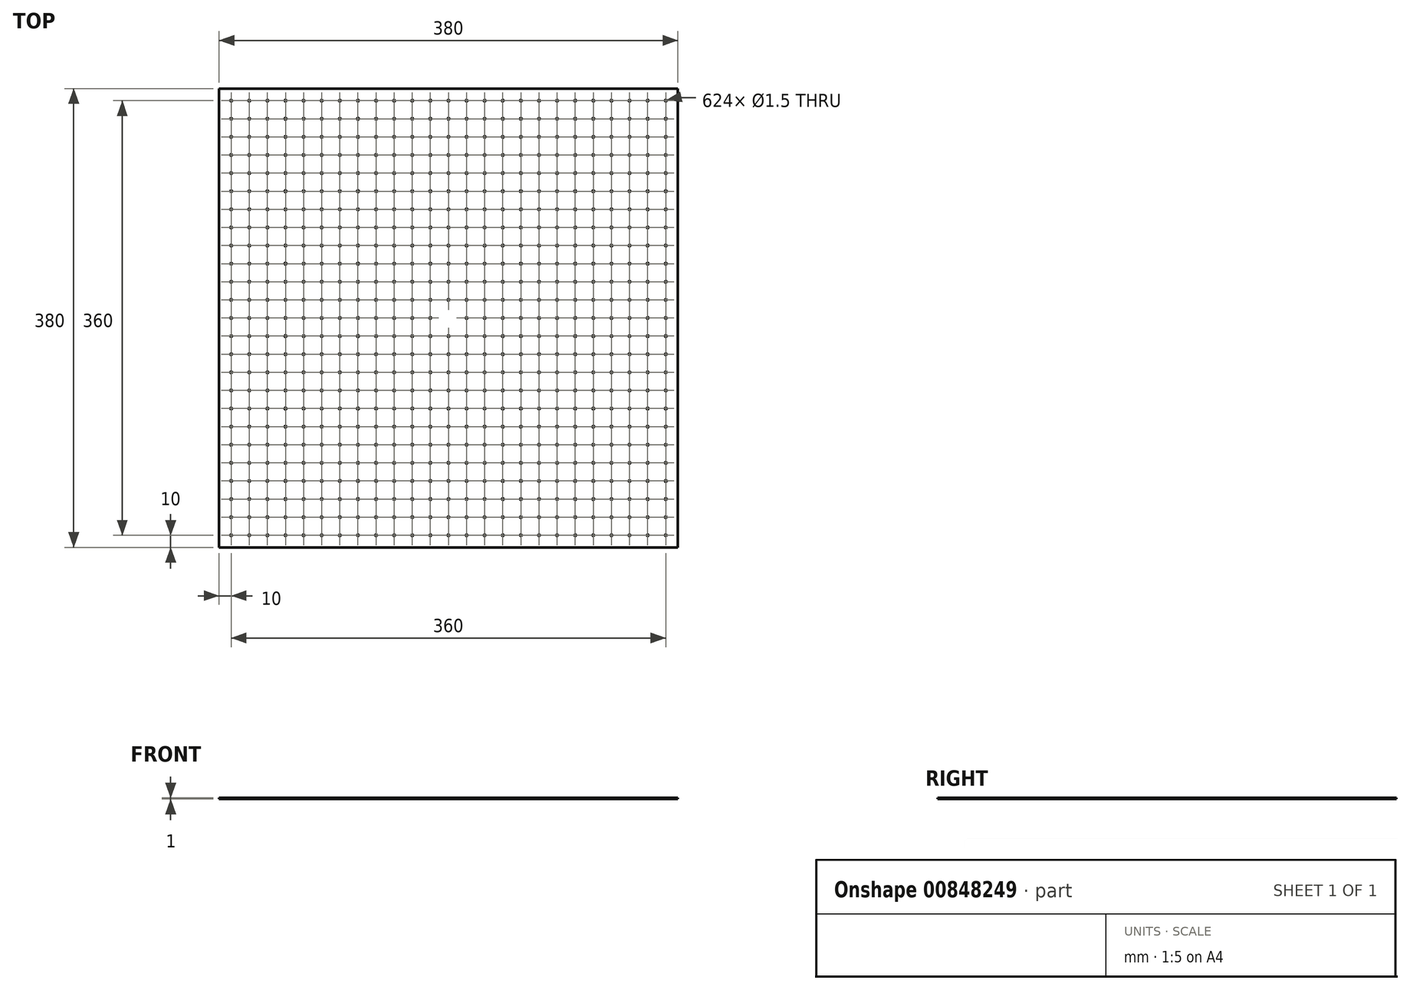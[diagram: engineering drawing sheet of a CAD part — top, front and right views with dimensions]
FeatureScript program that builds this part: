
annotation { "Feature Type Name" : "Feature", "Feature Type Description" : "" }
export const myFeature = defineFeature(function(context is Context, id is Id, definition is map)
    precondition{}
    {
        {
            var Q0;
            Q0=qCreatedBy(makeId("Top.planeOp"),FACE);
            var sketch = newSketch(context, id + "F0", { "sketchPlane" : qUnion([Q0])});
            skLineSegment(sketch, "E0.bottom", {"start": v(-190, -190) * mm, "end": v(190, -190) * mm});
            skLineSegment(sketch, "E0.top", {"start": v(-190, 190) * mm, "end": v(190, 190) * mm});
            skLineSegment(sketch, "E0.left", {"start": v(-190, -190) * mm, "end": v(-190, 190) * mm});
            skLineSegment(sketch, "E0.right", {"start": v(190, -190) * mm, "end": v(190, 190) * mm});
            skPoint(sketch, "E0.middle", {"position": v(0, 0) * mm});
            skSolve(sketch);
        }
        {
            var Q0;
            Q0 = qSketchRegion(id + "F0", true);
            extrude(context, id + "F1", {"entities" : qUnion([Q0]), "depth" : 1 * mm, "offsetDistance" : 25 * mm});
        }
        {
            var Q0;
            Q0=makeQuery(id+"F1.opExtrude","CAP_FACE",FACE,{"disambiguationData":[OSD([sQuery(id+"F0.wireOp",EDGE,"E0.bottom"),sQuery(id+"F0.wireOp",EDGE,"E0.top"),sQuery(id+"F0.wireOp",EDGE,"E0.left"),sQuery(id+"F0.wireOp",EDGE,"E0.right")])],"isStart":false});
            var sketch = newSketch(context, id + "F2", { "sketchPlane" : qUnion([Q0])});
            skCircle(sketch, "E1", {"center": v(-180, 180) * mm, "radius": 0.75 * mm});
            skCircle(sketch, "E2.1.0.0", {"center": v(-165, 180) * mm, "radius": 0.75 * mm});
            skCircle(sketch, "E2.2.0.0", {"center": v(-150, 180) * mm, "radius": 0.75 * mm});
            skCircle(sketch, "E2.3.0.0", {"center": v(-135, 180) * mm, "radius": 0.75 * mm});
            skCircle(sketch, "E2.4.0.0", {"center": v(-120, 180) * mm, "radius": 0.75 * mm});
            skCircle(sketch, "E2.5.0.0", {"center": v(-105, 180) * mm, "radius": 0.75 * mm});
            skCircle(sketch, "E2.6.0.0", {"center": v(-90, 180) * mm, "radius": 0.75 * mm});
            skCircle(sketch, "E2.7.0.0", {"center": v(-75, 180) * mm, "radius": 0.75 * mm});
            skCircle(sketch, "E2.8.0.0", {"center": v(-60, 180) * mm, "radius": 0.75 * mm});
            skCircle(sketch, "E2.9.0.0", {"center": v(-45, 180) * mm, "radius": 0.75 * mm});
            skCircle(sketch, "E2.10.0.0", {"center": v(-30, 180) * mm, "radius": 0.75 * mm});
            skCircle(sketch, "E2.11.0.0", {"center": v(-15, 180) * mm, "radius": 0.75 * mm});
            skCircle(sketch, "E2.12.0.0", {"center": v(0, 180) * mm, "radius": 0.75 * mm});
            skCircle(sketch, "E2.13.0.0", {"center": v(15, 180) * mm, "radius": 0.75 * mm});
            skCircle(sketch, "E2.14.0.0", {"center": v(30, 180) * mm, "radius": 0.75 * mm});
            skCircle(sketch, "E2.15.0.0", {"center": v(45, 180) * mm, "radius": 0.75 * mm});
            skCircle(sketch, "E2.16.0.0", {"center": v(60, 180) * mm, "radius": 0.75 * mm});
            skCircle(sketch, "E2.17.0.0", {"center": v(75, 180) * mm, "radius": 0.75 * mm});
            skCircle(sketch, "E2.18.0.0", {"center": v(90, 180) * mm, "radius": 0.75 * mm});
            skCircle(sketch, "E2.19.0.0", {"center": v(105, 180) * mm, "radius": 0.75 * mm});
            skCircle(sketch, "E2.20.0.0", {"center": v(120, 180) * mm, "radius": 0.75 * mm});
            skCircle(sketch, "E2.21.0.0", {"center": v(135, 180) * mm, "radius": 0.75 * mm});
            skCircle(sketch, "E2.22.0.0", {"center": v(150, 180) * mm, "radius": 0.75 * mm});
            skCircle(sketch, "E2.23.0.0", {"center": v(165, 180) * mm, "radius": 0.75 * mm});
            skCircle(sketch, "E2.24.0.0", {"center": v(180, 180) * mm, "radius": 0.75 * mm});
            skCircle(sketch, "E2.25.0.0", {"center": v(195, 180) * mm, "radius": 0.75 * mm});
            skCircle(sketch, "E2.26.0.0", {"center": v(210, 180) * mm, "radius": 0.75 * mm});
            skCircle(sketch, "E2.27.0.0", {"center": v(225, 180) * mm, "radius": 0.75 * mm});
            skCircle(sketch, "E2.28.0.0", {"center": v(240, 180) * mm, "radius": 0.75 * mm});
            skCircle(sketch, "E2.29.0.0", {"center": v(255, 180) * mm, "radius": 0.75 * mm});
            skCircle(sketch, "E2.30.0.0", {"center": v(270, 180) * mm, "radius": 0.75 * mm});
            skCircle(sketch, "E2.31.0.0", {"center": v(285, 180) * mm, "radius": 0.75 * mm});
            skCircle(sketch, "E2.32.0.0", {"center": v(300, 180) * mm, "radius": 0.75 * mm});
            skCircle(sketch, "E2.33.0.0", {"center": v(315, 180) * mm, "radius": 0.75 * mm});
            skCircle(sketch, "E2.34.0.0", {"center": v(330, 180) * mm, "radius": 0.75 * mm});
            skCircle(sketch, "E2.35.0.0", {"center": v(345, 180) * mm, "radius": 0.75 * mm});
            skLineSegment(sketch, "E2.direction1", {"start": v(-180, 180) * mm, "end": v(-165, 180) * mm, "construction": true});
            skCircle(sketch, "E3.0.1.0", {"center": v(-180, 165) * mm, "radius": 0.75 * mm});
            skCircle(sketch, "E3.0.1.1", {"center": v(-165, 165) * mm, "radius": 0.75 * mm});
            skCircle(sketch, "E3.0.1.2", {"center": v(-150, 165) * mm, "radius": 0.75 * mm});
            skCircle(sketch, "E3.0.1.3", {"center": v(-135, 165) * mm, "radius": 0.75 * mm});
            skCircle(sketch, "E3.0.1.4", {"center": v(-120, 165) * mm, "radius": 0.75 * mm});
            skCircle(sketch, "E3.0.1.5", {"center": v(-105, 165) * mm, "radius": 0.75 * mm});
            skCircle(sketch, "E3.0.1.6", {"center": v(-90, 165) * mm, "radius": 0.75 * mm});
            skCircle(sketch, "E3.0.1.7", {"center": v(-75, 165) * mm, "radius": 0.75 * mm});
            skCircle(sketch, "E3.0.1.8", {"center": v(-60, 165) * mm, "radius": 0.75 * mm});
            skCircle(sketch, "E3.0.1.9", {"center": v(-45, 165) * mm, "radius": 0.75 * mm});
            skCircle(sketch, "E3.0.1.10", {"center": v(-30, 165) * mm, "radius": 0.75 * mm});
            skCircle(sketch, "E3.0.1.11", {"center": v(-15, 165) * mm, "radius": 0.75 * mm});
            skCircle(sketch, "E3.0.1.12", {"center": v(0, 165) * mm, "radius": 0.75 * mm});
            skCircle(sketch, "E3.0.1.13", {"center": v(15, 165) * mm, "radius": 0.75 * mm});
            skCircle(sketch, "E3.0.1.14", {"center": v(30, 165) * mm, "radius": 0.75 * mm});
            skCircle(sketch, "E3.0.1.15", {"center": v(45, 165) * mm, "radius": 0.75 * mm});
            skCircle(sketch, "E3.0.1.16", {"center": v(60, 165) * mm, "radius": 0.75 * mm});
            skCircle(sketch, "E3.0.1.17", {"center": v(75, 165) * mm, "radius": 0.75 * mm});
            skCircle(sketch, "E3.0.1.18", {"center": v(90, 165) * mm, "radius": 0.75 * mm});
            skCircle(sketch, "E3.0.1.19", {"center": v(105, 165) * mm, "radius": 0.75 * mm});
            skCircle(sketch, "E3.0.1.20", {"center": v(120, 165) * mm, "radius": 0.75 * mm});
            skCircle(sketch, "E3.0.1.21", {"center": v(135, 165) * mm, "radius": 0.75 * mm});
            skCircle(sketch, "E3.0.1.22", {"center": v(150, 165) * mm, "radius": 0.75 * mm});
            skCircle(sketch, "E3.0.1.23", {"center": v(165, 165) * mm, "radius": 0.75 * mm});
            skCircle(sketch, "E3.0.1.24", {"center": v(180, 165) * mm, "radius": 0.75 * mm});
            skCircle(sketch, "E3.0.1.25", {"center": v(195, 165) * mm, "radius": 0.75 * mm});
            skCircle(sketch, "E3.0.1.26", {"center": v(210, 165) * mm, "radius": 0.75 * mm});
            skCircle(sketch, "E3.0.1.27", {"center": v(225, 165) * mm, "radius": 0.75 * mm});
            skCircle(sketch, "E3.0.1.28", {"center": v(240, 165) * mm, "radius": 0.75 * mm});
            skCircle(sketch, "E3.0.1.29", {"center": v(255, 165) * mm, "radius": 0.75 * mm});
            skCircle(sketch, "E3.0.1.30", {"center": v(270, 165) * mm, "radius": 0.75 * mm});
            skCircle(sketch, "E3.0.1.31", {"center": v(285, 165) * mm, "radius": 0.75 * mm});
            skCircle(sketch, "E3.0.1.32", {"center": v(300, 165) * mm, "radius": 0.75 * mm});
            skCircle(sketch, "E3.0.1.33", {"center": v(315, 165) * mm, "radius": 0.75 * mm});
            skCircle(sketch, "E3.0.1.34", {"center": v(345, 165) * mm, "radius": 0.75 * mm});
            skCircle(sketch, "E3.0.1.35", {"center": v(330, 165) * mm, "radius": 0.75 * mm});
            skLineSegment(sketch, "E3.direction1", {"start": v(-180, 180) * mm, "end": v(25, 180) * mm, "construction": true});
            skLineSegment(sketch, "E3.direction2", {"start": v(-180, 165) * mm, "end": v(-180, 180) * mm, "construction": true});
            skCircle(sketch, "E4.0.0.2", {"center": v(-180, 150) * mm, "radius": 0.75 * mm});
            skCircle(sketch, "E4.2.0.2", {"center": v(-165, 150) * mm, "radius": 0.75 * mm});
            skCircle(sketch, "E4.4.0.2", {"center": v(-150, 150) * mm, "radius": 0.75 * mm});
            skCircle(sketch, "E4.6.0.2", {"center": v(-135, 150) * mm, "radius": 0.75 * mm});
            skCircle(sketch, "E4.8.0.2", {"center": v(-120, 150) * mm, "radius": 0.75 * mm});
            skCircle(sketch, "E4.10.0.2", {"center": v(-105, 150) * mm, "radius": 0.75 * mm});
            skCircle(sketch, "E4.12.0.2", {"center": v(-90, 150) * mm, "radius": 0.75 * mm});
            skCircle(sketch, "E4.14.0.2", {"center": v(-75, 150) * mm, "radius": 0.75 * mm});
            skCircle(sketch, "E4.16.0.2", {"center": v(-60, 150) * mm, "radius": 0.75 * mm});
            skCircle(sketch, "E4.18.0.2", {"center": v(-45, 150) * mm, "radius": 0.75 * mm});
            skCircle(sketch, "E4.20.0.2", {"center": v(-30, 150) * mm, "radius": 0.75 * mm});
            skCircle(sketch, "E4.22.0.2", {"center": v(-15, 150) * mm, "radius": 0.75 * mm});
            skCircle(sketch, "E4.24.0.2", {"center": v(0, 150) * mm, "radius": 0.75 * mm});
            skCircle(sketch, "E4.26.0.2", {"center": v(15, 150) * mm, "radius": 0.75 * mm});
            skCircle(sketch, "E4.28.0.2", {"center": v(30, 150) * mm, "radius": 0.75 * mm});
            skCircle(sketch, "E4.30.0.2", {"center": v(45, 150) * mm, "radius": 0.75 * mm});
            skCircle(sketch, "E4.32.0.2", {"center": v(60, 150) * mm, "radius": 0.75 * mm});
            skCircle(sketch, "E4.34.0.2", {"center": v(75, 150) * mm, "radius": 0.75 * mm});
            skCircle(sketch, "E4.36.0.2", {"center": v(90, 150) * mm, "radius": 0.75 * mm});
            skCircle(sketch, "E4.38.0.2", {"center": v(105, 150) * mm, "radius": 0.75 * mm});
            skCircle(sketch, "E4.40.0.2", {"center": v(120, 150) * mm, "radius": 0.75 * mm});
            skCircle(sketch, "E4.42.0.2", {"center": v(135, 150) * mm, "radius": 0.75 * mm});
            skCircle(sketch, "E4.44.0.2", {"center": v(150, 150) * mm, "radius": 0.75 * mm});
            skCircle(sketch, "E4.46.0.2", {"center": v(165, 150) * mm, "radius": 0.75 * mm});
            skCircle(sketch, "E4.48.0.2", {"center": v(180, 150) * mm, "radius": 0.75 * mm});
            skCircle(sketch, "E4.50.0.2", {"center": v(195, 150) * mm, "radius": 0.75 * mm});
            skCircle(sketch, "E4.52.0.2", {"center": v(210, 150) * mm, "radius": 0.75 * mm});
            skCircle(sketch, "E4.54.0.2", {"center": v(225, 150) * mm, "radius": 0.75 * mm});
            skCircle(sketch, "E4.56.0.2", {"center": v(240, 150) * mm, "radius": 0.75 * mm});
            skCircle(sketch, "E4.58.0.2", {"center": v(255, 150) * mm, "radius": 0.75 * mm});
            skCircle(sketch, "E4.60.0.2", {"center": v(270, 150) * mm, "radius": 0.75 * mm});
            skCircle(sketch, "E4.62.0.2", {"center": v(285, 150) * mm, "radius": 0.75 * mm});
            skCircle(sketch, "E4.64.0.2", {"center": v(300, 150) * mm, "radius": 0.75 * mm});
            skCircle(sketch, "E4.66.0.2", {"center": v(315, 150) * mm, "radius": 0.75 * mm});
            skCircle(sketch, "E4.68.0.2", {"center": v(345, 150) * mm, "radius": 0.75 * mm});
            skCircle(sketch, "E4.70.0.2", {"center": v(330, 150) * mm, "radius": 0.75 * mm});
            skCircle(sketch, "E4.0.0.3", {"center": v(-180, 135) * mm, "radius": 0.75 * mm});
            skCircle(sketch, "E4.2.0.3", {"center": v(-165, 135) * mm, "radius": 0.75 * mm});
            skCircle(sketch, "E4.4.0.3", {"center": v(-150, 135) * mm, "radius": 0.75 * mm});
            skCircle(sketch, "E4.6.0.3", {"center": v(-135, 135) * mm, "radius": 0.75 * mm});
            skCircle(sketch, "E4.8.0.3", {"center": v(-120, 135) * mm, "radius": 0.75 * mm});
            skCircle(sketch, "E4.10.0.3", {"center": v(-105, 135) * mm, "radius": 0.75 * mm});
            skCircle(sketch, "E4.12.0.3", {"center": v(-90, 135) * mm, "radius": 0.75 * mm});
            skCircle(sketch, "E4.14.0.3", {"center": v(-75, 135) * mm, "radius": 0.75 * mm});
            skCircle(sketch, "E4.16.0.3", {"center": v(-60, 135) * mm, "radius": 0.75 * mm});
            skCircle(sketch, "E4.18.0.3", {"center": v(-45, 135) * mm, "radius": 0.75 * mm});
            skCircle(sketch, "E4.20.0.3", {"center": v(-30, 135) * mm, "radius": 0.75 * mm});
            skCircle(sketch, "E4.22.0.3", {"center": v(-15, 135) * mm, "radius": 0.75 * mm});
            skCircle(sketch, "E4.24.0.3", {"center": v(0, 135) * mm, "radius": 0.75 * mm});
            skCircle(sketch, "E4.26.0.3", {"center": v(15, 135) * mm, "radius": 0.75 * mm});
            skCircle(sketch, "E4.28.0.3", {"center": v(30, 135) * mm, "radius": 0.75 * mm});
            skCircle(sketch, "E4.30.0.3", {"center": v(45, 135) * mm, "radius": 0.75 * mm});
            skCircle(sketch, "E4.32.0.3", {"center": v(60, 135) * mm, "radius": 0.75 * mm});
            skCircle(sketch, "E4.34.0.3", {"center": v(75, 135) * mm, "radius": 0.75 * mm});
            skCircle(sketch, "E4.36.0.3", {"center": v(90, 135) * mm, "radius": 0.75 * mm});
            skCircle(sketch, "E4.38.0.3", {"center": v(105, 135) * mm, "radius": 0.75 * mm});
            skCircle(sketch, "E4.40.0.3", {"center": v(120, 135) * mm, "radius": 0.75 * mm});
            skCircle(sketch, "E4.42.0.3", {"center": v(135, 135) * mm, "radius": 0.75 * mm});
            skCircle(sketch, "E4.44.0.3", {"center": v(150, 135) * mm, "radius": 0.75 * mm});
            skCircle(sketch, "E4.46.0.3", {"center": v(165, 135) * mm, "radius": 0.75 * mm});
            skCircle(sketch, "E4.48.0.3", {"center": v(180, 135) * mm, "radius": 0.75 * mm});
            skCircle(sketch, "E4.50.0.3", {"center": v(195, 135) * mm, "radius": 0.75 * mm});
            skCircle(sketch, "E4.52.0.3", {"center": v(210, 135) * mm, "radius": 0.75 * mm});
            skCircle(sketch, "E4.54.0.3", {"center": v(225, 135) * mm, "radius": 0.75 * mm});
            skCircle(sketch, "E4.56.0.3", {"center": v(240, 135) * mm, "radius": 0.75 * mm});
            skCircle(sketch, "E4.58.0.3", {"center": v(255, 135) * mm, "radius": 0.75 * mm});
            skCircle(sketch, "E4.60.0.3", {"center": v(270, 135) * mm, "radius": 0.75 * mm});
            skCircle(sketch, "E4.62.0.3", {"center": v(285, 135) * mm, "radius": 0.75 * mm});
            skCircle(sketch, "E4.64.0.3", {"center": v(300, 135) * mm, "radius": 0.75 * mm});
            skCircle(sketch, "E4.66.0.3", {"center": v(315, 135) * mm, "radius": 0.75 * mm});
            skCircle(sketch, "E4.68.0.3", {"center": v(345, 135) * mm, "radius": 0.75 * mm});
            skCircle(sketch, "E4.70.0.3", {"center": v(330, 135) * mm, "radius": 0.75 * mm});
            skCircle(sketch, "E4.0.0.4", {"center": v(-180, 120) * mm, "radius": 0.75 * mm});
            skCircle(sketch, "E4.2.0.4", {"center": v(-165, 120) * mm, "radius": 0.75 * mm});
            skCircle(sketch, "E4.4.0.4", {"center": v(-150, 120) * mm, "radius": 0.75 * mm});
            skCircle(sketch, "E4.6.0.4", {"center": v(-135, 120) * mm, "radius": 0.75 * mm});
            skCircle(sketch, "E4.8.0.4", {"center": v(-120, 120) * mm, "radius": 0.75 * mm});
            skCircle(sketch, "E4.10.0.4", {"center": v(-105, 120) * mm, "radius": 0.75 * mm});
            skCircle(sketch, "E4.12.0.4", {"center": v(-90, 120) * mm, "radius": 0.75 * mm});
            skCircle(sketch, "E4.14.0.4", {"center": v(-75, 120) * mm, "radius": 0.75 * mm});
            skCircle(sketch, "E4.16.0.4", {"center": v(-60, 120) * mm, "radius": 0.75 * mm});
            skCircle(sketch, "E4.18.0.4", {"center": v(-45, 120) * mm, "radius": 0.75 * mm});
            skCircle(sketch, "E4.20.0.4", {"center": v(-30, 120) * mm, "radius": 0.75 * mm});
            skCircle(sketch, "E4.22.0.4", {"center": v(-15, 120) * mm, "radius": 0.75 * mm});
            skCircle(sketch, "E4.24.0.4", {"center": v(0, 120) * mm, "radius": 0.75 * mm});
            skCircle(sketch, "E4.26.0.4", {"center": v(15, 120) * mm, "radius": 0.75 * mm});
            skCircle(sketch, "E4.28.0.4", {"center": v(30, 120) * mm, "radius": 0.75 * mm});
            skCircle(sketch, "E4.30.0.4", {"center": v(45, 120) * mm, "radius": 0.75 * mm});
            skCircle(sketch, "E4.32.0.4", {"center": v(60, 120) * mm, "radius": 0.75 * mm});
            skCircle(sketch, "E4.34.0.4", {"center": v(75, 120) * mm, "radius": 0.75 * mm});
            skCircle(sketch, "E4.36.0.4", {"center": v(90, 120) * mm, "radius": 0.75 * mm});
            skCircle(sketch, "E4.38.0.4", {"center": v(105, 120) * mm, "radius": 0.75 * mm});
            skCircle(sketch, "E4.40.0.4", {"center": v(120, 120) * mm, "radius": 0.75 * mm});
            skCircle(sketch, "E4.42.0.4", {"center": v(135, 120) * mm, "radius": 0.75 * mm});
            skCircle(sketch, "E4.44.0.4", {"center": v(150, 120) * mm, "radius": 0.75 * mm});
            skCircle(sketch, "E4.46.0.4", {"center": v(165, 120) * mm, "radius": 0.75 * mm});
            skCircle(sketch, "E4.48.0.4", {"center": v(180, 120) * mm, "radius": 0.75 * mm});
            skCircle(sketch, "E4.50.0.4", {"center": v(195, 120) * mm, "radius": 0.75 * mm});
            skCircle(sketch, "E4.52.0.4", {"center": v(210, 120) * mm, "radius": 0.75 * mm});
            skCircle(sketch, "E4.54.0.4", {"center": v(225, 120) * mm, "radius": 0.75 * mm});
            skCircle(sketch, "E4.56.0.4", {"center": v(240, 120) * mm, "radius": 0.75 * mm});
            skCircle(sketch, "E4.58.0.4", {"center": v(255, 120) * mm, "radius": 0.75 * mm});
            skCircle(sketch, "E4.60.0.4", {"center": v(270, 120) * mm, "radius": 0.75 * mm});
            skCircle(sketch, "E4.62.0.4", {"center": v(285, 120) * mm, "radius": 0.75 * mm});
            skCircle(sketch, "E4.64.0.4", {"center": v(300, 120) * mm, "radius": 0.75 * mm});
            skCircle(sketch, "E4.66.0.4", {"center": v(315, 120) * mm, "radius": 0.75 * mm});
            skCircle(sketch, "E4.68.0.4", {"center": v(345, 120) * mm, "radius": 0.75 * mm});
            skCircle(sketch, "E4.70.0.4", {"center": v(330, 120) * mm, "radius": 0.75 * mm});
            skCircle(sketch, "E4.0.0.5", {"center": v(-180, 105) * mm, "radius": 0.75 * mm});
            skCircle(sketch, "E4.2.0.5", {"center": v(-165, 105) * mm, "radius": 0.75 * mm});
            skCircle(sketch, "E4.4.0.5", {"center": v(-150, 105) * mm, "radius": 0.75 * mm});
            skCircle(sketch, "E4.6.0.5", {"center": v(-135, 105) * mm, "radius": 0.75 * mm});
            skCircle(sketch, "E4.8.0.5", {"center": v(-120, 105) * mm, "radius": 0.75 * mm});
            skCircle(sketch, "E4.10.0.5", {"center": v(-105, 105) * mm, "radius": 0.75 * mm});
            skCircle(sketch, "E4.12.0.5", {"center": v(-90, 105) * mm, "radius": 0.75 * mm});
            skCircle(sketch, "E4.14.0.5", {"center": v(-75, 105) * mm, "radius": 0.75 * mm});
            skCircle(sketch, "E4.16.0.5", {"center": v(-60, 105) * mm, "radius": 0.75 * mm});
            skCircle(sketch, "E4.18.0.5", {"center": v(-45, 105) * mm, "radius": 0.75 * mm});
            skCircle(sketch, "E4.20.0.5", {"center": v(-30, 105) * mm, "radius": 0.75 * mm});
            skCircle(sketch, "E4.22.0.5", {"center": v(-15, 105) * mm, "radius": 0.75 * mm});
            skCircle(sketch, "E4.24.0.5", {"center": v(0, 105) * mm, "radius": 0.75 * mm});
            skCircle(sketch, "E4.26.0.5", {"center": v(15, 105) * mm, "radius": 0.75 * mm});
            skCircle(sketch, "E4.28.0.5", {"center": v(30, 105) * mm, "radius": 0.75 * mm});
            skCircle(sketch, "E4.30.0.5", {"center": v(45, 105) * mm, "radius": 0.75 * mm});
            skCircle(sketch, "E4.32.0.5", {"center": v(60, 105) * mm, "radius": 0.75 * mm});
            skCircle(sketch, "E4.34.0.5", {"center": v(75, 105) * mm, "radius": 0.75 * mm});
            skCircle(sketch, "E4.36.0.5", {"center": v(90, 105) * mm, "radius": 0.75 * mm});
            skCircle(sketch, "E4.38.0.5", {"center": v(105, 105) * mm, "radius": 0.75 * mm});
            skCircle(sketch, "E4.40.0.5", {"center": v(120, 105) * mm, "radius": 0.75 * mm});
            skCircle(sketch, "E4.42.0.5", {"center": v(135, 105) * mm, "radius": 0.75 * mm});
            skCircle(sketch, "E4.44.0.5", {"center": v(150, 105) * mm, "radius": 0.75 * mm});
            skCircle(sketch, "E4.46.0.5", {"center": v(165, 105) * mm, "radius": 0.75 * mm});
            skCircle(sketch, "E4.48.0.5", {"center": v(180, 105) * mm, "radius": 0.75 * mm});
            skCircle(sketch, "E4.50.0.5", {"center": v(195, 105) * mm, "radius": 0.75 * mm});
            skCircle(sketch, "E4.52.0.5", {"center": v(210, 105) * mm, "radius": 0.75 * mm});
            skCircle(sketch, "E4.54.0.5", {"center": v(225, 105) * mm, "radius": 0.75 * mm});
            skCircle(sketch, "E4.56.0.5", {"center": v(240, 105) * mm, "radius": 0.75 * mm});
            skCircle(sketch, "E4.58.0.5", {"center": v(255, 105) * mm, "radius": 0.75 * mm});
            skCircle(sketch, "E4.60.0.5", {"center": v(270, 105) * mm, "radius": 0.75 * mm});
            skCircle(sketch, "E4.62.0.5", {"center": v(285, 105) * mm, "radius": 0.75 * mm});
            skCircle(sketch, "E4.64.0.5", {"center": v(300, 105) * mm, "radius": 0.75 * mm});
            skCircle(sketch, "E4.66.0.5", {"center": v(315, 105) * mm, "radius": 0.75 * mm});
            skCircle(sketch, "E4.68.0.5", {"center": v(345, 105) * mm, "radius": 0.75 * mm});
            skCircle(sketch, "E4.70.0.5", {"center": v(330, 105) * mm, "radius": 0.75 * mm});
            skCircle(sketch, "E4.0.0.6", {"center": v(-180, 90) * mm, "radius": 0.75 * mm});
            skCircle(sketch, "E4.2.0.6", {"center": v(-165, 90) * mm, "radius": 0.75 * mm});
            skCircle(sketch, "E4.4.0.6", {"center": v(-150, 90) * mm, "radius": 0.75 * mm});
            skCircle(sketch, "E4.6.0.6", {"center": v(-135, 90) * mm, "radius": 0.75 * mm});
            skCircle(sketch, "E4.8.0.6", {"center": v(-120, 90) * mm, "radius": 0.75 * mm});
            skCircle(sketch, "E4.10.0.6", {"center": v(-105, 90) * mm, "radius": 0.75 * mm});
            skCircle(sketch, "E4.12.0.6", {"center": v(-90, 90) * mm, "radius": 0.75 * mm});
            skCircle(sketch, "E4.14.0.6", {"center": v(-75, 90) * mm, "radius": 0.75 * mm});
            skCircle(sketch, "E4.16.0.6", {"center": v(-60, 90) * mm, "radius": 0.75 * mm});
            skCircle(sketch, "E4.18.0.6", {"center": v(-45, 90) * mm, "radius": 0.75 * mm});
            skCircle(sketch, "E4.20.0.6", {"center": v(-30, 90) * mm, "radius": 0.75 * mm});
            skCircle(sketch, "E4.22.0.6", {"center": v(-15, 90) * mm, "radius": 0.75 * mm});
            skCircle(sketch, "E4.24.0.6", {"center": v(0, 90) * mm, "radius": 0.75 * mm});
            skCircle(sketch, "E4.26.0.6", {"center": v(15, 90) * mm, "radius": 0.75 * mm});
            skCircle(sketch, "E4.28.0.6", {"center": v(30, 90) * mm, "radius": 0.75 * mm});
            skCircle(sketch, "E4.30.0.6", {"center": v(45, 90) * mm, "radius": 0.75 * mm});
            skCircle(sketch, "E4.32.0.6", {"center": v(60, 90) * mm, "radius": 0.75 * mm});
            skCircle(sketch, "E4.34.0.6", {"center": v(75, 90) * mm, "radius": 0.75 * mm});
            skCircle(sketch, "E4.36.0.6", {"center": v(90, 90) * mm, "radius": 0.75 * mm});
            skCircle(sketch, "E4.38.0.6", {"center": v(105, 90) * mm, "radius": 0.75 * mm});
            skCircle(sketch, "E4.40.0.6", {"center": v(120, 90) * mm, "radius": 0.75 * mm});
            skCircle(sketch, "E4.42.0.6", {"center": v(135, 90) * mm, "radius": 0.75 * mm});
            skCircle(sketch, "E4.44.0.6", {"center": v(150, 90) * mm, "radius": 0.75 * mm});
            skCircle(sketch, "E4.46.0.6", {"center": v(165, 90) * mm, "radius": 0.75 * mm});
            skCircle(sketch, "E4.48.0.6", {"center": v(180, 90) * mm, "radius": 0.75 * mm});
            skCircle(sketch, "E4.50.0.6", {"center": v(195, 90) * mm, "radius": 0.75 * mm});
            skCircle(sketch, "E4.52.0.6", {"center": v(210, 90) * mm, "radius": 0.75 * mm});
            skCircle(sketch, "E4.54.0.6", {"center": v(225, 90) * mm, "radius": 0.75 * mm});
            skCircle(sketch, "E4.56.0.6", {"center": v(240, 90) * mm, "radius": 0.75 * mm});
            skCircle(sketch, "E4.58.0.6", {"center": v(255, 90) * mm, "radius": 0.75 * mm});
            skCircle(sketch, "E4.60.0.6", {"center": v(270, 90) * mm, "radius": 0.75 * mm});
            skCircle(sketch, "E4.62.0.6", {"center": v(285, 90) * mm, "radius": 0.75 * mm});
            skCircle(sketch, "E4.64.0.6", {"center": v(300, 90) * mm, "radius": 0.75 * mm});
            skCircle(sketch, "E4.66.0.6", {"center": v(315, 90) * mm, "radius": 0.75 * mm});
            skCircle(sketch, "E4.68.0.6", {"center": v(345, 90) * mm, "radius": 0.75 * mm});
            skCircle(sketch, "E4.70.0.6", {"center": v(330, 90) * mm, "radius": 0.75 * mm});
            skCircle(sketch, "E4.0.0.7", {"center": v(-180, 75) * mm, "radius": 0.75 * mm});
            skCircle(sketch, "E4.2.0.7", {"center": v(-165, 75) * mm, "radius": 0.75 * mm});
            skCircle(sketch, "E4.4.0.7", {"center": v(-150, 75) * mm, "radius": 0.75 * mm});
            skCircle(sketch, "E4.6.0.7", {"center": v(-135, 75) * mm, "radius": 0.75 * mm});
            skCircle(sketch, "E4.8.0.7", {"center": v(-120, 75) * mm, "radius": 0.75 * mm});
            skCircle(sketch, "E4.10.0.7", {"center": v(-105, 75) * mm, "radius": 0.75 * mm});
            skCircle(sketch, "E4.12.0.7", {"center": v(-90, 75) * mm, "radius": 0.75 * mm});
            skCircle(sketch, "E4.14.0.7", {"center": v(-75, 75) * mm, "radius": 0.75 * mm});
            skCircle(sketch, "E4.16.0.7", {"center": v(-60, 75) * mm, "radius": 0.75 * mm});
            skCircle(sketch, "E4.18.0.7", {"center": v(-45, 75) * mm, "radius": 0.75 * mm});
            skCircle(sketch, "E4.20.0.7", {"center": v(-30, 75) * mm, "radius": 0.75 * mm});
            skCircle(sketch, "E4.22.0.7", {"center": v(-15, 75) * mm, "radius": 0.75 * mm});
            skCircle(sketch, "E4.24.0.7", {"center": v(0, 75) * mm, "radius": 0.75 * mm});
            skCircle(sketch, "E4.26.0.7", {"center": v(15, 75) * mm, "radius": 0.75 * mm});
            skCircle(sketch, "E4.28.0.7", {"center": v(30, 75) * mm, "radius": 0.75 * mm});
            skCircle(sketch, "E4.30.0.7", {"center": v(45, 75) * mm, "radius": 0.75 * mm});
            skCircle(sketch, "E4.32.0.7", {"center": v(60, 75) * mm, "radius": 0.75 * mm});
            skCircle(sketch, "E4.34.0.7", {"center": v(75, 75) * mm, "radius": 0.75 * mm});
            skCircle(sketch, "E4.36.0.7", {"center": v(90, 75) * mm, "radius": 0.75 * mm});
            skCircle(sketch, "E4.38.0.7", {"center": v(105, 75) * mm, "radius": 0.75 * mm});
            skCircle(sketch, "E4.40.0.7", {"center": v(120, 75) * mm, "radius": 0.75 * mm});
            skCircle(sketch, "E4.42.0.7", {"center": v(135, 75) * mm, "radius": 0.75 * mm});
            skCircle(sketch, "E4.44.0.7", {"center": v(150, 75) * mm, "radius": 0.75 * mm});
            skCircle(sketch, "E4.46.0.7", {"center": v(165, 75) * mm, "radius": 0.75 * mm});
            skCircle(sketch, "E4.48.0.7", {"center": v(180, 75) * mm, "radius": 0.75 * mm});
            skCircle(sketch, "E4.50.0.7", {"center": v(195, 75) * mm, "radius": 0.75 * mm});
            skCircle(sketch, "E4.52.0.7", {"center": v(210, 75) * mm, "radius": 0.75 * mm});
            skCircle(sketch, "E4.54.0.7", {"center": v(225, 75) * mm, "radius": 0.75 * mm});
            skCircle(sketch, "E4.56.0.7", {"center": v(240, 75) * mm, "radius": 0.75 * mm});
            skCircle(sketch, "E4.58.0.7", {"center": v(255, 75) * mm, "radius": 0.75 * mm});
            skCircle(sketch, "E4.60.0.7", {"center": v(270, 75) * mm, "radius": 0.75 * mm});
            skCircle(sketch, "E4.62.0.7", {"center": v(285, 75) * mm, "radius": 0.75 * mm});
            skCircle(sketch, "E4.64.0.7", {"center": v(300, 75) * mm, "radius": 0.75 * mm});
            skCircle(sketch, "E4.66.0.7", {"center": v(315, 75) * mm, "radius": 0.75 * mm});
            skCircle(sketch, "E4.68.0.7", {"center": v(345, 75) * mm, "radius": 0.75 * mm});
            skCircle(sketch, "E4.70.0.7", {"center": v(330, 75) * mm, "radius": 0.75 * mm});
            skCircle(sketch, "E4.0.0.8", {"center": v(-180, 60) * mm, "radius": 0.75 * mm});
            skCircle(sketch, "E4.2.0.8", {"center": v(-165, 60) * mm, "radius": 0.75 * mm});
            skCircle(sketch, "E4.4.0.8", {"center": v(-150, 60) * mm, "radius": 0.75 * mm});
            skCircle(sketch, "E4.6.0.8", {"center": v(-135, 60) * mm, "radius": 0.75 * mm});
            skCircle(sketch, "E4.8.0.8", {"center": v(-120, 60) * mm, "radius": 0.75 * mm});
            skCircle(sketch, "E4.10.0.8", {"center": v(-105, 60) * mm, "radius": 0.75 * mm});
            skCircle(sketch, "E4.12.0.8", {"center": v(-90, 60) * mm, "radius": 0.75 * mm});
            skCircle(sketch, "E4.14.0.8", {"center": v(-75, 60) * mm, "radius": 0.75 * mm});
            skCircle(sketch, "E4.16.0.8", {"center": v(-60, 60) * mm, "radius": 0.75 * mm});
            skCircle(sketch, "E4.18.0.8", {"center": v(-45, 60) * mm, "radius": 0.75 * mm});
            skCircle(sketch, "E4.20.0.8", {"center": v(-30, 60) * mm, "radius": 0.75 * mm});
            skCircle(sketch, "E4.22.0.8", {"center": v(-15, 60) * mm, "radius": 0.75 * mm});
            skCircle(sketch, "E4.24.0.8", {"center": v(0, 60) * mm, "radius": 0.75 * mm});
            skCircle(sketch, "E4.26.0.8", {"center": v(15, 60) * mm, "radius": 0.75 * mm});
            skCircle(sketch, "E4.28.0.8", {"center": v(30, 60) * mm, "radius": 0.75 * mm});
            skCircle(sketch, "E4.30.0.8", {"center": v(45, 60) * mm, "radius": 0.75 * mm});
            skCircle(sketch, "E4.32.0.8", {"center": v(60, 60) * mm, "radius": 0.75 * mm});
            skCircle(sketch, "E4.34.0.8", {"center": v(75, 60) * mm, "radius": 0.75 * mm});
            skCircle(sketch, "E4.36.0.8", {"center": v(90, 60) * mm, "radius": 0.75 * mm});
            skCircle(sketch, "E4.38.0.8", {"center": v(105, 60) * mm, "radius": 0.75 * mm});
            skCircle(sketch, "E4.40.0.8", {"center": v(120, 60) * mm, "radius": 0.75 * mm});
            skCircle(sketch, "E4.42.0.8", {"center": v(135, 60) * mm, "radius": 0.75 * mm});
            skCircle(sketch, "E4.44.0.8", {"center": v(150, 60) * mm, "radius": 0.75 * mm});
            skCircle(sketch, "E4.46.0.8", {"center": v(165, 60) * mm, "radius": 0.75 * mm});
            skCircle(sketch, "E4.48.0.8", {"center": v(180, 60) * mm, "radius": 0.75 * mm});
            skCircle(sketch, "E4.50.0.8", {"center": v(195, 60) * mm, "radius": 0.75 * mm});
            skCircle(sketch, "E4.52.0.8", {"center": v(210, 60) * mm, "radius": 0.75 * mm});
            skCircle(sketch, "E4.54.0.8", {"center": v(225, 60) * mm, "radius": 0.75 * mm});
            skCircle(sketch, "E4.56.0.8", {"center": v(240, 60) * mm, "radius": 0.75 * mm});
            skCircle(sketch, "E4.58.0.8", {"center": v(255, 60) * mm, "radius": 0.75 * mm});
            skCircle(sketch, "E4.60.0.8", {"center": v(270, 60) * mm, "radius": 0.75 * mm});
            skCircle(sketch, "E4.62.0.8", {"center": v(285, 60) * mm, "radius": 0.75 * mm});
            skCircle(sketch, "E4.64.0.8", {"center": v(300, 60) * mm, "radius": 0.75 * mm});
            skCircle(sketch, "E4.66.0.8", {"center": v(315, 60) * mm, "radius": 0.75 * mm});
            skCircle(sketch, "E4.68.0.8", {"center": v(345, 60) * mm, "radius": 0.75 * mm});
            skCircle(sketch, "E4.70.0.8", {"center": v(330, 60) * mm, "radius": 0.75 * mm});
            skCircle(sketch, "E4.0.0.9", {"center": v(-180, 45) * mm, "radius": 0.75 * mm});
            skCircle(sketch, "E4.2.0.9", {"center": v(-165, 45) * mm, "radius": 0.75 * mm});
            skCircle(sketch, "E4.4.0.9", {"center": v(-150, 45) * mm, "radius": 0.75 * mm});
            skCircle(sketch, "E4.6.0.9", {"center": v(-135, 45) * mm, "radius": 0.75 * mm});
            skCircle(sketch, "E4.8.0.9", {"center": v(-120, 45) * mm, "radius": 0.75 * mm});
            skCircle(sketch, "E4.10.0.9", {"center": v(-105, 45) * mm, "radius": 0.75 * mm});
            skCircle(sketch, "E4.12.0.9", {"center": v(-90, 45) * mm, "radius": 0.75 * mm});
            skCircle(sketch, "E4.14.0.9", {"center": v(-75, 45) * mm, "radius": 0.75 * mm});
            skCircle(sketch, "E4.16.0.9", {"center": v(-60, 45) * mm, "radius": 0.75 * mm});
            skCircle(sketch, "E4.18.0.9", {"center": v(-45, 45) * mm, "radius": 0.75 * mm});
            skCircle(sketch, "E4.20.0.9", {"center": v(-30, 45) * mm, "radius": 0.75 * mm});
            skCircle(sketch, "E4.22.0.9", {"center": v(-15, 45) * mm, "radius": 0.75 * mm});
            skCircle(sketch, "E4.24.0.9", {"center": v(0, 45) * mm, "radius": 0.75 * mm});
            skCircle(sketch, "E4.26.0.9", {"center": v(15, 45) * mm, "radius": 0.75 * mm});
            skCircle(sketch, "E4.28.0.9", {"center": v(30, 45) * mm, "radius": 0.75 * mm});
            skCircle(sketch, "E4.30.0.9", {"center": v(45, 45) * mm, "radius": 0.75 * mm});
            skCircle(sketch, "E4.32.0.9", {"center": v(60, 45) * mm, "radius": 0.75 * mm});
            skCircle(sketch, "E4.34.0.9", {"center": v(75, 45) * mm, "radius": 0.75 * mm});
            skCircle(sketch, "E4.36.0.9", {"center": v(90, 45) * mm, "radius": 0.75 * mm});
            skCircle(sketch, "E4.38.0.9", {"center": v(105, 45) * mm, "radius": 0.75 * mm});
            skCircle(sketch, "E4.40.0.9", {"center": v(120, 45) * mm, "radius": 0.75 * mm});
            skCircle(sketch, "E4.42.0.9", {"center": v(135, 45) * mm, "radius": 0.75 * mm});
            skCircle(sketch, "E4.44.0.9", {"center": v(150, 45) * mm, "radius": 0.75 * mm});
            skCircle(sketch, "E4.46.0.9", {"center": v(165, 45) * mm, "radius": 0.75 * mm});
            skCircle(sketch, "E4.48.0.9", {"center": v(180, 45) * mm, "radius": 0.75 * mm});
            skCircle(sketch, "E4.50.0.9", {"center": v(195, 45) * mm, "radius": 0.75 * mm});
            skCircle(sketch, "E4.52.0.9", {"center": v(210, 45) * mm, "radius": 0.75 * mm});
            skCircle(sketch, "E4.54.0.9", {"center": v(225, 45) * mm, "radius": 0.75 * mm});
            skCircle(sketch, "E4.56.0.9", {"center": v(240, 45) * mm, "radius": 0.75 * mm});
            skCircle(sketch, "E4.58.0.9", {"center": v(255, 45) * mm, "radius": 0.75 * mm});
            skCircle(sketch, "E4.60.0.9", {"center": v(270, 45) * mm, "radius": 0.75 * mm});
            skCircle(sketch, "E4.62.0.9", {"center": v(285, 45) * mm, "radius": 0.75 * mm});
            skCircle(sketch, "E4.64.0.9", {"center": v(300, 45) * mm, "radius": 0.75 * mm});
            skCircle(sketch, "E4.66.0.9", {"center": v(315, 45) * mm, "radius": 0.75 * mm});
            skCircle(sketch, "E4.68.0.9", {"center": v(345, 45) * mm, "radius": 0.75 * mm});
            skCircle(sketch, "E4.70.0.9", {"center": v(330, 45) * mm, "radius": 0.75 * mm});
            skCircle(sketch, "E4.0.0.10", {"center": v(-180, 30) * mm, "radius": 0.75 * mm});
            skCircle(sketch, "E4.2.0.10", {"center": v(-165, 30) * mm, "radius": 0.75 * mm});
            skCircle(sketch, "E4.4.0.10", {"center": v(-150, 30) * mm, "radius": 0.75 * mm});
            skCircle(sketch, "E4.6.0.10", {"center": v(-135, 30) * mm, "radius": 0.75 * mm});
            skCircle(sketch, "E4.8.0.10", {"center": v(-120, 30) * mm, "radius": 0.75 * mm});
            skCircle(sketch, "E4.10.0.10", {"center": v(-105, 30) * mm, "radius": 0.75 * mm});
            skCircle(sketch, "E4.12.0.10", {"center": v(-90, 30) * mm, "radius": 0.75 * mm});
            skCircle(sketch, "E4.14.0.10", {"center": v(-75, 30) * mm, "radius": 0.75 * mm});
            skCircle(sketch, "E4.16.0.10", {"center": v(-60, 30) * mm, "radius": 0.75 * mm});
            skCircle(sketch, "E4.18.0.10", {"center": v(-45, 30) * mm, "radius": 0.75 * mm});
            skCircle(sketch, "E4.20.0.10", {"center": v(-30, 30) * mm, "radius": 0.75 * mm});
            skCircle(sketch, "E4.22.0.10", {"center": v(-15, 30) * mm, "radius": 0.75 * mm});
            skCircle(sketch, "E4.24.0.10", {"center": v(0, 30) * mm, "radius": 0.75 * mm});
            skCircle(sketch, "E4.26.0.10", {"center": v(15, 30) * mm, "radius": 0.75 * mm});
            skCircle(sketch, "E4.28.0.10", {"center": v(30, 30) * mm, "radius": 0.75 * mm});
            skCircle(sketch, "E4.30.0.10", {"center": v(45, 30) * mm, "radius": 0.75 * mm});
            skCircle(sketch, "E4.32.0.10", {"center": v(60, 30) * mm, "radius": 0.75 * mm});
            skCircle(sketch, "E4.34.0.10", {"center": v(75, 30) * mm, "radius": 0.75 * mm});
            skCircle(sketch, "E4.36.0.10", {"center": v(90, 30) * mm, "radius": 0.75 * mm});
            skCircle(sketch, "E4.38.0.10", {"center": v(105, 30) * mm, "radius": 0.75 * mm});
            skCircle(sketch, "E4.40.0.10", {"center": v(120, 30) * mm, "radius": 0.75 * mm});
            skCircle(sketch, "E4.42.0.10", {"center": v(135, 30) * mm, "radius": 0.75 * mm});
            skCircle(sketch, "E4.44.0.10", {"center": v(150, 30) * mm, "radius": 0.75 * mm});
            skCircle(sketch, "E4.46.0.10", {"center": v(165, 30) * mm, "radius": 0.75 * mm});
            skCircle(sketch, "E4.48.0.10", {"center": v(180, 30) * mm, "radius": 0.75 * mm});
            skCircle(sketch, "E4.50.0.10", {"center": v(195, 30) * mm, "radius": 0.75 * mm});
            skCircle(sketch, "E4.52.0.10", {"center": v(210, 30) * mm, "radius": 0.75 * mm});
            skCircle(sketch, "E4.54.0.10", {"center": v(225, 30) * mm, "radius": 0.75 * mm});
            skCircle(sketch, "E4.56.0.10", {"center": v(240, 30) * mm, "radius": 0.75 * mm});
            skCircle(sketch, "E4.58.0.10", {"center": v(255, 30) * mm, "radius": 0.75 * mm});
            skCircle(sketch, "E4.60.0.10", {"center": v(270, 30) * mm, "radius": 0.75 * mm});
            skCircle(sketch, "E4.62.0.10", {"center": v(285, 30) * mm, "radius": 0.75 * mm});
            skCircle(sketch, "E4.64.0.10", {"center": v(300, 30) * mm, "radius": 0.75 * mm});
            skCircle(sketch, "E4.66.0.10", {"center": v(315, 30) * mm, "radius": 0.75 * mm});
            skCircle(sketch, "E4.68.0.10", {"center": v(345, 30) * mm, "radius": 0.75 * mm});
            skCircle(sketch, "E4.70.0.10", {"center": v(330, 30) * mm, "radius": 0.75 * mm});
            skCircle(sketch, "E4.0.0.11", {"center": v(-180, 15) * mm, "radius": 0.75 * mm});
            skCircle(sketch, "E4.2.0.11", {"center": v(-165, 15) * mm, "radius": 0.75 * mm});
            skCircle(sketch, "E4.4.0.11", {"center": v(-150, 15) * mm, "radius": 0.75 * mm});
            skCircle(sketch, "E4.6.0.11", {"center": v(-135, 15) * mm, "radius": 0.75 * mm});
            skCircle(sketch, "E4.8.0.11", {"center": v(-120, 15) * mm, "radius": 0.75 * mm});
            skCircle(sketch, "E4.10.0.11", {"center": v(-105, 15) * mm, "radius": 0.75 * mm});
            skCircle(sketch, "E4.12.0.11", {"center": v(-90, 15) * mm, "radius": 0.75 * mm});
            skCircle(sketch, "E4.14.0.11", {"center": v(-75, 15) * mm, "radius": 0.75 * mm});
            skCircle(sketch, "E4.16.0.11", {"center": v(-60, 15) * mm, "radius": 0.75 * mm});
            skCircle(sketch, "E4.18.0.11", {"center": v(-45, 15) * mm, "radius": 0.75 * mm});
            skCircle(sketch, "E4.20.0.11", {"center": v(-30, 15) * mm, "radius": 0.75 * mm});
            skCircle(sketch, "E4.22.0.11", {"center": v(-15, 15) * mm, "radius": 0.75 * mm});
            skCircle(sketch, "E4.24.0.11", {"center": v(0, 15) * mm, "radius": 0.75 * mm});
            skCircle(sketch, "E4.26.0.11", {"center": v(15, 15) * mm, "radius": 0.75 * mm});
            skCircle(sketch, "E4.28.0.11", {"center": v(30, 15) * mm, "radius": 0.75 * mm});
            skCircle(sketch, "E4.30.0.11", {"center": v(45, 15) * mm, "radius": 0.75 * mm});
            skCircle(sketch, "E4.32.0.11", {"center": v(60, 15) * mm, "radius": 0.75 * mm});
            skCircle(sketch, "E4.34.0.11", {"center": v(75, 15) * mm, "radius": 0.75 * mm});
            skCircle(sketch, "E4.36.0.11", {"center": v(90, 15) * mm, "radius": 0.75 * mm});
            skCircle(sketch, "E4.38.0.11", {"center": v(105, 15) * mm, "radius": 0.75 * mm});
            skCircle(sketch, "E4.40.0.11", {"center": v(120, 15) * mm, "radius": 0.75 * mm});
            skCircle(sketch, "E4.42.0.11", {"center": v(135, 15) * mm, "radius": 0.75 * mm});
            skCircle(sketch, "E4.44.0.11", {"center": v(150, 15) * mm, "radius": 0.75 * mm});
            skCircle(sketch, "E4.46.0.11", {"center": v(165, 15) * mm, "radius": 0.75 * mm});
            skCircle(sketch, "E4.48.0.11", {"center": v(180, 15) * mm, "radius": 0.75 * mm});
            skCircle(sketch, "E4.50.0.11", {"center": v(195, 15) * mm, "radius": 0.75 * mm});
            skCircle(sketch, "E4.52.0.11", {"center": v(210, 15) * mm, "radius": 0.75 * mm});
            skCircle(sketch, "E4.54.0.11", {"center": v(225, 15) * mm, "radius": 0.75 * mm});
            skCircle(sketch, "E4.56.0.11", {"center": v(240, 15) * mm, "radius": 0.75 * mm});
            skCircle(sketch, "E4.58.0.11", {"center": v(255, 15) * mm, "radius": 0.75 * mm});
            skCircle(sketch, "E4.60.0.11", {"center": v(270, 15) * mm, "radius": 0.75 * mm});
            skCircle(sketch, "E4.62.0.11", {"center": v(285, 15) * mm, "radius": 0.75 * mm});
            skCircle(sketch, "E4.64.0.11", {"center": v(300, 15) * mm, "radius": 0.75 * mm});
            skCircle(sketch, "E4.66.0.11", {"center": v(315, 15) * mm, "radius": 0.75 * mm});
            skCircle(sketch, "E4.68.0.11", {"center": v(345, 15) * mm, "radius": 0.75 * mm});
            skCircle(sketch, "E4.70.0.11", {"center": v(330, 15) * mm, "radius": 0.75 * mm});
            skCircle(sketch, "E4.0.0.12", {"center": v(-180, 0) * mm, "radius": 0.75 * mm});
            skCircle(sketch, "E4.2.0.12", {"center": v(-165, 0) * mm, "radius": 0.75 * mm});
            skCircle(sketch, "E4.4.0.12", {"center": v(-150, 0) * mm, "radius": 0.75 * mm});
            skCircle(sketch, "E4.6.0.12", {"center": v(-135, 0) * mm, "radius": 0.75 * mm});
            skCircle(sketch, "E4.8.0.12", {"center": v(-120, 0) * mm, "radius": 0.75 * mm});
            skCircle(sketch, "E4.10.0.12", {"center": v(-105, 0) * mm, "radius": 0.75 * mm});
            skCircle(sketch, "E4.12.0.12", {"center": v(-90, 0) * mm, "radius": 0.75 * mm});
            skCircle(sketch, "E4.14.0.12", {"center": v(-75, 0) * mm, "radius": 0.75 * mm});
            skCircle(sketch, "E4.16.0.12", {"center": v(-60, 0) * mm, "radius": 0.75 * mm});
            skCircle(sketch, "E4.18.0.12", {"center": v(-45, 0) * mm, "radius": 0.75 * mm});
            skCircle(sketch, "E4.20.0.12", {"center": v(-30, 0) * mm, "radius": 0.75 * mm});
            skCircle(sketch, "E4.22.0.12", {"center": v(-15, 0) * mm, "radius": 0.75 * mm});
            skCircle(sketch, "E4.24.0.12", {"center": v(0, 0) * mm, "radius": 0.75 * mm});
            skCircle(sketch, "E4.26.0.12", {"center": v(15, 0) * mm, "radius": 0.75 * mm});
            skCircle(sketch, "E4.28.0.12", {"center": v(30, 0) * mm, "radius": 0.75 * mm});
            skCircle(sketch, "E4.30.0.12", {"center": v(45, 0) * mm, "radius": 0.75 * mm});
            skCircle(sketch, "E4.32.0.12", {"center": v(60, 0) * mm, "radius": 0.75 * mm});
            skCircle(sketch, "E4.34.0.12", {"center": v(75, 0) * mm, "radius": 0.75 * mm});
            skCircle(sketch, "E4.36.0.12", {"center": v(90, 0) * mm, "radius": 0.75 * mm});
            skCircle(sketch, "E4.38.0.12", {"center": v(105, 0) * mm, "radius": 0.75 * mm});
            skCircle(sketch, "E4.40.0.12", {"center": v(120, 0) * mm, "radius": 0.75 * mm});
            skCircle(sketch, "E4.42.0.12", {"center": v(135, 0) * mm, "radius": 0.75 * mm});
            skCircle(sketch, "E4.44.0.12", {"center": v(150, 0) * mm, "radius": 0.75 * mm});
            skCircle(sketch, "E4.46.0.12", {"center": v(165, 0) * mm, "radius": 0.75 * mm});
            skCircle(sketch, "E4.48.0.12", {"center": v(180, 0) * mm, "radius": 0.75 * mm});
            skCircle(sketch, "E4.50.0.12", {"center": v(195, 0) * mm, "radius": 0.75 * mm});
            skCircle(sketch, "E4.52.0.12", {"center": v(210, 0) * mm, "radius": 0.75 * mm});
            skCircle(sketch, "E4.54.0.12", {"center": v(225, 0) * mm, "radius": 0.75 * mm});
            skCircle(sketch, "E4.56.0.12", {"center": v(240, 0) * mm, "radius": 0.75 * mm});
            skCircle(sketch, "E4.58.0.12", {"center": v(255, 0) * mm, "radius": 0.75 * mm});
            skCircle(sketch, "E4.60.0.12", {"center": v(270, 0) * mm, "radius": 0.75 * mm});
            skCircle(sketch, "E4.62.0.12", {"center": v(285, 0) * mm, "radius": 0.75 * mm});
            skCircle(sketch, "E4.64.0.12", {"center": v(300, 0) * mm, "radius": 0.75 * mm});
            skCircle(sketch, "E4.66.0.12", {"center": v(315, 0) * mm, "radius": 0.75 * mm});
            skCircle(sketch, "E4.68.0.12", {"center": v(345, 0) * mm, "radius": 0.75 * mm});
            skCircle(sketch, "E4.70.0.12", {"center": v(330, 0) * mm, "radius": 0.75 * mm});
            skCircle(sketch, "E4.0.0.13", {"center": v(-180, -15) * mm, "radius": 0.75 * mm});
            skCircle(sketch, "E4.2.0.13", {"center": v(-165, -15) * mm, "radius": 0.75 * mm});
            skCircle(sketch, "E4.4.0.13", {"center": v(-150, -15) * mm, "radius": 0.75 * mm});
            skCircle(sketch, "E4.6.0.13", {"center": v(-135, -15) * mm, "radius": 0.75 * mm});
            skCircle(sketch, "E4.8.0.13", {"center": v(-120, -15) * mm, "radius": 0.75 * mm});
            skCircle(sketch, "E4.10.0.13", {"center": v(-105, -15) * mm, "radius": 0.75 * mm});
            skCircle(sketch, "E4.12.0.13", {"center": v(-90, -15) * mm, "radius": 0.75 * mm});
            skCircle(sketch, "E4.14.0.13", {"center": v(-75, -15) * mm, "radius": 0.75 * mm});
            skCircle(sketch, "E4.16.0.13", {"center": v(-60, -15) * mm, "radius": 0.75 * mm});
            skCircle(sketch, "E4.18.0.13", {"center": v(-45, -15) * mm, "radius": 0.75 * mm});
            skCircle(sketch, "E4.20.0.13", {"center": v(-30, -15) * mm, "radius": 0.75 * mm});
            skCircle(sketch, "E4.22.0.13", {"center": v(-15, -15) * mm, "radius": 0.75 * mm});
            skCircle(sketch, "E4.24.0.13", {"center": v(0, -15) * mm, "radius": 0.75 * mm});
            skCircle(sketch, "E4.26.0.13", {"center": v(15, -15) * mm, "radius": 0.75 * mm});
            skCircle(sketch, "E4.28.0.13", {"center": v(30, -15) * mm, "radius": 0.75 * mm});
            skCircle(sketch, "E4.30.0.13", {"center": v(45, -15) * mm, "radius": 0.75 * mm});
            skCircle(sketch, "E4.32.0.13", {"center": v(60, -15) * mm, "radius": 0.75 * mm});
            skCircle(sketch, "E4.34.0.13", {"center": v(75, -15) * mm, "radius": 0.75 * mm});
            skCircle(sketch, "E4.36.0.13", {"center": v(90, -15) * mm, "radius": 0.75 * mm});
            skCircle(sketch, "E4.38.0.13", {"center": v(105, -15) * mm, "radius": 0.75 * mm});
            skCircle(sketch, "E4.40.0.13", {"center": v(120, -15) * mm, "radius": 0.75 * mm});
            skCircle(sketch, "E4.42.0.13", {"center": v(135, -15) * mm, "radius": 0.75 * mm});
            skCircle(sketch, "E4.44.0.13", {"center": v(150, -15) * mm, "radius": 0.75 * mm});
            skCircle(sketch, "E4.46.0.13", {"center": v(165, -15) * mm, "radius": 0.75 * mm});
            skCircle(sketch, "E4.48.0.13", {"center": v(180, -15) * mm, "radius": 0.75 * mm});
            skCircle(sketch, "E4.50.0.13", {"center": v(195, -15) * mm, "radius": 0.75 * mm});
            skCircle(sketch, "E4.52.0.13", {"center": v(210, -15) * mm, "radius": 0.75 * mm});
            skCircle(sketch, "E4.54.0.13", {"center": v(225, -15) * mm, "radius": 0.75 * mm});
            skCircle(sketch, "E4.56.0.13", {"center": v(240, -15) * mm, "radius": 0.75 * mm});
            skCircle(sketch, "E4.58.0.13", {"center": v(255, -15) * mm, "radius": 0.75 * mm});
            skCircle(sketch, "E4.60.0.13", {"center": v(270, -15) * mm, "radius": 0.75 * mm});
            skCircle(sketch, "E4.62.0.13", {"center": v(285, -15) * mm, "radius": 0.75 * mm});
            skCircle(sketch, "E4.64.0.13", {"center": v(300, -15) * mm, "radius": 0.75 * mm});
            skCircle(sketch, "E4.66.0.13", {"center": v(315, -15) * mm, "radius": 0.75 * mm});
            skCircle(sketch, "E4.68.0.13", {"center": v(345, -15) * mm, "radius": 0.75 * mm});
            skCircle(sketch, "E4.70.0.13", {"center": v(330, -15) * mm, "radius": 0.75 * mm});
            skCircle(sketch, "E4.0.0.14", {"center": v(-180, -30) * mm, "radius": 0.75 * mm});
            skCircle(sketch, "E4.2.0.14", {"center": v(-165, -30) * mm, "radius": 0.75 * mm});
            skCircle(sketch, "E4.4.0.14", {"center": v(-150, -30) * mm, "radius": 0.75 * mm});
            skCircle(sketch, "E4.6.0.14", {"center": v(-135, -30) * mm, "radius": 0.75 * mm});
            skCircle(sketch, "E4.8.0.14", {"center": v(-120, -30) * mm, "radius": 0.75 * mm});
            skCircle(sketch, "E4.10.0.14", {"center": v(-105, -30) * mm, "radius": 0.75 * mm});
            skCircle(sketch, "E4.12.0.14", {"center": v(-90, -30) * mm, "radius": 0.75 * mm});
            skCircle(sketch, "E4.14.0.14", {"center": v(-75, -30) * mm, "radius": 0.75 * mm});
            skCircle(sketch, "E4.16.0.14", {"center": v(-60, -30) * mm, "radius": 0.75 * mm});
            skCircle(sketch, "E4.18.0.14", {"center": v(-45, -30) * mm, "radius": 0.75 * mm});
            skCircle(sketch, "E4.20.0.14", {"center": v(-30, -30) * mm, "radius": 0.75 * mm});
            skCircle(sketch, "E4.22.0.14", {"center": v(-15, -30) * mm, "radius": 0.75 * mm});
            skCircle(sketch, "E4.24.0.14", {"center": v(0, -30) * mm, "radius": 0.75 * mm});
            skCircle(sketch, "E4.26.0.14", {"center": v(15, -30) * mm, "radius": 0.75 * mm});
            skCircle(sketch, "E4.28.0.14", {"center": v(30, -30) * mm, "radius": 0.75 * mm});
            skCircle(sketch, "E4.30.0.14", {"center": v(45, -30) * mm, "radius": 0.75 * mm});
            skCircle(sketch, "E4.32.0.14", {"center": v(60, -30) * mm, "radius": 0.75 * mm});
            skCircle(sketch, "E4.34.0.14", {"center": v(75, -30) * mm, "radius": 0.75 * mm});
            skCircle(sketch, "E4.36.0.14", {"center": v(90, -30) * mm, "radius": 0.75 * mm});
            skCircle(sketch, "E4.38.0.14", {"center": v(105, -30) * mm, "radius": 0.75 * mm});
            skCircle(sketch, "E4.40.0.14", {"center": v(120, -30) * mm, "radius": 0.75 * mm});
            skCircle(sketch, "E4.42.0.14", {"center": v(135, -30) * mm, "radius": 0.75 * mm});
            skCircle(sketch, "E4.44.0.14", {"center": v(150, -30) * mm, "radius": 0.75 * mm});
            skCircle(sketch, "E4.46.0.14", {"center": v(165, -30) * mm, "radius": 0.75 * mm});
            skCircle(sketch, "E4.48.0.14", {"center": v(180, -30) * mm, "radius": 0.75 * mm});
            skCircle(sketch, "E4.50.0.14", {"center": v(195, -30) * mm, "radius": 0.75 * mm});
            skCircle(sketch, "E4.52.0.14", {"center": v(210, -30) * mm, "radius": 0.75 * mm});
            skCircle(sketch, "E4.54.0.14", {"center": v(225, -30) * mm, "radius": 0.75 * mm});
            skCircle(sketch, "E4.56.0.14", {"center": v(240, -30) * mm, "radius": 0.75 * mm});
            skCircle(sketch, "E4.58.0.14", {"center": v(255, -30) * mm, "radius": 0.75 * mm});
            skCircle(sketch, "E4.60.0.14", {"center": v(270, -30) * mm, "radius": 0.75 * mm});
            skCircle(sketch, "E4.62.0.14", {"center": v(285, -30) * mm, "radius": 0.75 * mm});
            skCircle(sketch, "E4.64.0.14", {"center": v(300, -30) * mm, "radius": 0.75 * mm});
            skCircle(sketch, "E4.66.0.14", {"center": v(315, -30) * mm, "radius": 0.75 * mm});
            skCircle(sketch, "E4.68.0.14", {"center": v(345, -30) * mm, "radius": 0.75 * mm});
            skCircle(sketch, "E4.70.0.14", {"center": v(330, -30) * mm, "radius": 0.75 * mm});
            skCircle(sketch, "E4.0.0.15", {"center": v(-180, -45) * mm, "radius": 0.75 * mm});
            skCircle(sketch, "E4.2.0.15", {"center": v(-165, -45) * mm, "radius": 0.75 * mm});
            skCircle(sketch, "E4.4.0.15", {"center": v(-150, -45) * mm, "radius": 0.75 * mm});
            skCircle(sketch, "E4.6.0.15", {"center": v(-135, -45) * mm, "radius": 0.75 * mm});
            skCircle(sketch, "E4.8.0.15", {"center": v(-120, -45) * mm, "radius": 0.75 * mm});
            skCircle(sketch, "E4.10.0.15", {"center": v(-105, -45) * mm, "radius": 0.75 * mm});
            skCircle(sketch, "E4.12.0.15", {"center": v(-90, -45) * mm, "radius": 0.75 * mm});
            skCircle(sketch, "E4.14.0.15", {"center": v(-75, -45) * mm, "radius": 0.75 * mm});
            skCircle(sketch, "E4.16.0.15", {"center": v(-60, -45) * mm, "radius": 0.75 * mm});
            skCircle(sketch, "E4.18.0.15", {"center": v(-45, -45) * mm, "radius": 0.75 * mm});
            skCircle(sketch, "E4.20.0.15", {"center": v(-30, -45) * mm, "radius": 0.75 * mm});
            skCircle(sketch, "E4.22.0.15", {"center": v(-15, -45) * mm, "radius": 0.75 * mm});
            skCircle(sketch, "E4.24.0.15", {"center": v(0, -45) * mm, "radius": 0.75 * mm});
            skCircle(sketch, "E4.26.0.15", {"center": v(15, -45) * mm, "radius": 0.75 * mm});
            skCircle(sketch, "E4.28.0.15", {"center": v(30, -45) * mm, "radius": 0.75 * mm});
            skCircle(sketch, "E4.30.0.15", {"center": v(45, -45) * mm, "radius": 0.75 * mm});
            skCircle(sketch, "E4.32.0.15", {"center": v(60, -45) * mm, "radius": 0.75 * mm});
            skCircle(sketch, "E4.34.0.15", {"center": v(75, -45) * mm, "radius": 0.75 * mm});
            skCircle(sketch, "E4.36.0.15", {"center": v(90, -45) * mm, "radius": 0.75 * mm});
            skCircle(sketch, "E4.38.0.15", {"center": v(105, -45) * mm, "radius": 0.75 * mm});
            skCircle(sketch, "E4.40.0.15", {"center": v(120, -45) * mm, "radius": 0.75 * mm});
            skCircle(sketch, "E4.42.0.15", {"center": v(135, -45) * mm, "radius": 0.75 * mm});
            skCircle(sketch, "E4.44.0.15", {"center": v(150, -45) * mm, "radius": 0.75 * mm});
            skCircle(sketch, "E4.46.0.15", {"center": v(165, -45) * mm, "radius": 0.75 * mm});
            skCircle(sketch, "E4.48.0.15", {"center": v(180, -45) * mm, "radius": 0.75 * mm});
            skCircle(sketch, "E4.50.0.15", {"center": v(195, -45) * mm, "radius": 0.75 * mm});
            skCircle(sketch, "E4.52.0.15", {"center": v(210, -45) * mm, "radius": 0.75 * mm});
            skCircle(sketch, "E4.54.0.15", {"center": v(225, -45) * mm, "radius": 0.75 * mm});
            skCircle(sketch, "E4.56.0.15", {"center": v(240, -45) * mm, "radius": 0.75 * mm});
            skCircle(sketch, "E4.58.0.15", {"center": v(255, -45) * mm, "radius": 0.75 * mm});
            skCircle(sketch, "E4.60.0.15", {"center": v(270, -45) * mm, "radius": 0.75 * mm});
            skCircle(sketch, "E4.62.0.15", {"center": v(285, -45) * mm, "radius": 0.75 * mm});
            skCircle(sketch, "E4.64.0.15", {"center": v(300, -45) * mm, "radius": 0.75 * mm});
            skCircle(sketch, "E4.66.0.15", {"center": v(315, -45) * mm, "radius": 0.75 * mm});
            skCircle(sketch, "E4.68.0.15", {"center": v(345, -45) * mm, "radius": 0.75 * mm});
            skCircle(sketch, "E4.70.0.15", {"center": v(330, -45) * mm, "radius": 0.75 * mm});
            skCircle(sketch, "E4.0.0.16", {"center": v(-180, -60) * mm, "radius": 0.75 * mm});
            skCircle(sketch, "E4.2.0.16", {"center": v(-165, -60) * mm, "radius": 0.75 * mm});
            skCircle(sketch, "E4.4.0.16", {"center": v(-150, -60) * mm, "radius": 0.75 * mm});
            skCircle(sketch, "E4.6.0.16", {"center": v(-135, -60) * mm, "radius": 0.75 * mm});
            skCircle(sketch, "E4.8.0.16", {"center": v(-120, -60) * mm, "radius": 0.75 * mm});
            skCircle(sketch, "E4.10.0.16", {"center": v(-105, -60) * mm, "radius": 0.75 * mm});
            skCircle(sketch, "E4.12.0.16", {"center": v(-90, -60) * mm, "radius": 0.75 * mm});
            skCircle(sketch, "E4.14.0.16", {"center": v(-75, -60) * mm, "radius": 0.75 * mm});
            skCircle(sketch, "E4.16.0.16", {"center": v(-60, -60) * mm, "radius": 0.75 * mm});
            skCircle(sketch, "E4.18.0.16", {"center": v(-45, -60) * mm, "radius": 0.75 * mm});
            skCircle(sketch, "E4.20.0.16", {"center": v(-30, -60) * mm, "radius": 0.75 * mm});
            skCircle(sketch, "E4.22.0.16", {"center": v(-15, -60) * mm, "radius": 0.75 * mm});
            skCircle(sketch, "E4.24.0.16", {"center": v(0, -60) * mm, "radius": 0.75 * mm});
            skCircle(sketch, "E4.26.0.16", {"center": v(15, -60) * mm, "radius": 0.75 * mm});
            skCircle(sketch, "E4.28.0.16", {"center": v(30, -60) * mm, "radius": 0.75 * mm});
            skCircle(sketch, "E4.30.0.16", {"center": v(45, -60) * mm, "radius": 0.75 * mm});
            skCircle(sketch, "E4.32.0.16", {"center": v(60, -60) * mm, "radius": 0.75 * mm});
            skCircle(sketch, "E4.34.0.16", {"center": v(75, -60) * mm, "radius": 0.75 * mm});
            skCircle(sketch, "E4.36.0.16", {"center": v(90, -60) * mm, "radius": 0.75 * mm});
            skCircle(sketch, "E4.38.0.16", {"center": v(105, -60) * mm, "radius": 0.75 * mm});
            skCircle(sketch, "E4.40.0.16", {"center": v(120, -60) * mm, "radius": 0.75 * mm});
            skCircle(sketch, "E4.42.0.16", {"center": v(135, -60) * mm, "radius": 0.75 * mm});
            skCircle(sketch, "E4.44.0.16", {"center": v(150, -60) * mm, "radius": 0.75 * mm});
            skCircle(sketch, "E4.46.0.16", {"center": v(165, -60) * mm, "radius": 0.75 * mm});
            skCircle(sketch, "E4.48.0.16", {"center": v(180, -60) * mm, "radius": 0.75 * mm});
            skCircle(sketch, "E4.50.0.16", {"center": v(195, -60) * mm, "radius": 0.75 * mm});
            skCircle(sketch, "E4.52.0.16", {"center": v(210, -60) * mm, "radius": 0.75 * mm});
            skCircle(sketch, "E4.54.0.16", {"center": v(225, -60) * mm, "radius": 0.75 * mm});
            skCircle(sketch, "E4.56.0.16", {"center": v(240, -60) * mm, "radius": 0.75 * mm});
            skCircle(sketch, "E4.58.0.16", {"center": v(255, -60) * mm, "radius": 0.75 * mm});
            skCircle(sketch, "E4.60.0.16", {"center": v(270, -60) * mm, "radius": 0.75 * mm});
            skCircle(sketch, "E4.62.0.16", {"center": v(285, -60) * mm, "radius": 0.75 * mm});
            skCircle(sketch, "E4.64.0.16", {"center": v(300, -60) * mm, "radius": 0.75 * mm});
            skCircle(sketch, "E4.66.0.16", {"center": v(315, -60) * mm, "radius": 0.75 * mm});
            skCircle(sketch, "E4.68.0.16", {"center": v(345, -60) * mm, "radius": 0.75 * mm});
            skCircle(sketch, "E4.70.0.16", {"center": v(330, -60) * mm, "radius": 0.75 * mm});
            skCircle(sketch, "E4.0.0.17", {"center": v(-180, -75) * mm, "radius": 0.75 * mm});
            skCircle(sketch, "E4.2.0.17", {"center": v(-165, -75) * mm, "radius": 0.75 * mm});
            skCircle(sketch, "E4.4.0.17", {"center": v(-150, -75) * mm, "radius": 0.75 * mm});
            skCircle(sketch, "E4.6.0.17", {"center": v(-135, -75) * mm, "radius": 0.75 * mm});
            skCircle(sketch, "E4.8.0.17", {"center": v(-120, -75) * mm, "radius": 0.75 * mm});
            skCircle(sketch, "E4.10.0.17", {"center": v(-105, -75) * mm, "radius": 0.75 * mm});
            skCircle(sketch, "E4.12.0.17", {"center": v(-90, -75) * mm, "radius": 0.75 * mm});
            skCircle(sketch, "E4.14.0.17", {"center": v(-75, -75) * mm, "radius": 0.75 * mm});
            skCircle(sketch, "E4.16.0.17", {"center": v(-60, -75) * mm, "radius": 0.75 * mm});
            skCircle(sketch, "E4.18.0.17", {"center": v(-45, -75) * mm, "radius": 0.75 * mm});
            skCircle(sketch, "E4.20.0.17", {"center": v(-30, -75) * mm, "radius": 0.75 * mm});
            skCircle(sketch, "E4.22.0.17", {"center": v(-15, -75) * mm, "radius": 0.75 * mm});
            skCircle(sketch, "E4.24.0.17", {"center": v(0, -75) * mm, "radius": 0.75 * mm});
            skCircle(sketch, "E4.26.0.17", {"center": v(15, -75) * mm, "radius": 0.75 * mm});
            skCircle(sketch, "E4.28.0.17", {"center": v(30, -75) * mm, "radius": 0.75 * mm});
            skCircle(sketch, "E4.30.0.17", {"center": v(45, -75) * mm, "radius": 0.75 * mm});
            skCircle(sketch, "E4.32.0.17", {"center": v(60, -75) * mm, "radius": 0.75 * mm});
            skCircle(sketch, "E4.34.0.17", {"center": v(75, -75) * mm, "radius": 0.75 * mm});
            skCircle(sketch, "E4.36.0.17", {"center": v(90, -75) * mm, "radius": 0.75 * mm});
            skCircle(sketch, "E4.38.0.17", {"center": v(105, -75) * mm, "radius": 0.75 * mm});
            skCircle(sketch, "E4.40.0.17", {"center": v(120, -75) * mm, "radius": 0.75 * mm});
            skCircle(sketch, "E4.42.0.17", {"center": v(135, -75) * mm, "radius": 0.75 * mm});
            skCircle(sketch, "E4.44.0.17", {"center": v(150, -75) * mm, "radius": 0.75 * mm});
            skCircle(sketch, "E4.46.0.17", {"center": v(165, -75) * mm, "radius": 0.75 * mm});
            skCircle(sketch, "E4.48.0.17", {"center": v(180, -75) * mm, "radius": 0.75 * mm});
            skCircle(sketch, "E4.50.0.17", {"center": v(195, -75) * mm, "radius": 0.75 * mm});
            skCircle(sketch, "E4.52.0.17", {"center": v(210, -75) * mm, "radius": 0.75 * mm});
            skCircle(sketch, "E4.54.0.17", {"center": v(225, -75) * mm, "radius": 0.75 * mm});
            skCircle(sketch, "E4.56.0.17", {"center": v(240, -75) * mm, "radius": 0.75 * mm});
            skCircle(sketch, "E4.58.0.17", {"center": v(255, -75) * mm, "radius": 0.75 * mm});
            skCircle(sketch, "E4.60.0.17", {"center": v(270, -75) * mm, "radius": 0.75 * mm});
            skCircle(sketch, "E4.62.0.17", {"center": v(285, -75) * mm, "radius": 0.75 * mm});
            skCircle(sketch, "E4.64.0.17", {"center": v(300, -75) * mm, "radius": 0.75 * mm});
            skCircle(sketch, "E4.66.0.17", {"center": v(315, -75) * mm, "radius": 0.75 * mm});
            skCircle(sketch, "E4.68.0.17", {"center": v(345, -75) * mm, "radius": 0.75 * mm});
            skCircle(sketch, "E4.70.0.17", {"center": v(330, -75) * mm, "radius": 0.75 * mm});
            skCircle(sketch, "E4.0.0.18", {"center": v(-180, -90) * mm, "radius": 0.75 * mm});
            skCircle(sketch, "E4.2.0.18", {"center": v(-165, -90) * mm, "radius": 0.75 * mm});
            skCircle(sketch, "E4.4.0.18", {"center": v(-150, -90) * mm, "radius": 0.75 * mm});
            skCircle(sketch, "E4.6.0.18", {"center": v(-135, -90) * mm, "radius": 0.75 * mm});
            skCircle(sketch, "E4.8.0.18", {"center": v(-120, -90) * mm, "radius": 0.75 * mm});
            skCircle(sketch, "E4.10.0.18", {"center": v(-105, -90) * mm, "radius": 0.75 * mm});
            skCircle(sketch, "E4.12.0.18", {"center": v(-90, -90) * mm, "radius": 0.75 * mm});
            skCircle(sketch, "E4.14.0.18", {"center": v(-75, -90) * mm, "radius": 0.75 * mm});
            skCircle(sketch, "E4.16.0.18", {"center": v(-60, -90) * mm, "radius": 0.75 * mm});
            skCircle(sketch, "E4.18.0.18", {"center": v(-45, -90) * mm, "radius": 0.75 * mm});
            skCircle(sketch, "E4.20.0.18", {"center": v(-30, -90) * mm, "radius": 0.75 * mm});
            skCircle(sketch, "E4.22.0.18", {"center": v(-15, -90) * mm, "radius": 0.75 * mm});
            skCircle(sketch, "E4.24.0.18", {"center": v(0, -90) * mm, "radius": 0.75 * mm});
            skCircle(sketch, "E4.26.0.18", {"center": v(15, -90) * mm, "radius": 0.75 * mm});
            skCircle(sketch, "E4.28.0.18", {"center": v(30, -90) * mm, "radius": 0.75 * mm});
            skCircle(sketch, "E4.30.0.18", {"center": v(45, -90) * mm, "radius": 0.75 * mm});
            skCircle(sketch, "E4.32.0.18", {"center": v(60, -90) * mm, "radius": 0.75 * mm});
            skCircle(sketch, "E4.34.0.18", {"center": v(75, -90) * mm, "radius": 0.75 * mm});
            skCircle(sketch, "E4.36.0.18", {"center": v(90, -90) * mm, "radius": 0.75 * mm});
            skCircle(sketch, "E4.38.0.18", {"center": v(105, -90) * mm, "radius": 0.75 * mm});
            skCircle(sketch, "E4.40.0.18", {"center": v(120, -90) * mm, "radius": 0.75 * mm});
            skCircle(sketch, "E4.42.0.18", {"center": v(135, -90) * mm, "radius": 0.75 * mm});
            skCircle(sketch, "E4.44.0.18", {"center": v(150, -90) * mm, "radius": 0.75 * mm});
            skCircle(sketch, "E4.46.0.18", {"center": v(165, -90) * mm, "radius": 0.75 * mm});
            skCircle(sketch, "E4.48.0.18", {"center": v(180, -90) * mm, "radius": 0.75 * mm});
            skCircle(sketch, "E4.50.0.18", {"center": v(195, -90) * mm, "radius": 0.75 * mm});
            skCircle(sketch, "E4.52.0.18", {"center": v(210, -90) * mm, "radius": 0.75 * mm});
            skCircle(sketch, "E4.54.0.18", {"center": v(225, -90) * mm, "radius": 0.75 * mm});
            skCircle(sketch, "E4.56.0.18", {"center": v(240, -90) * mm, "radius": 0.75 * mm});
            skCircle(sketch, "E4.58.0.18", {"center": v(255, -90) * mm, "radius": 0.75 * mm});
            skCircle(sketch, "E4.60.0.18", {"center": v(270, -90) * mm, "radius": 0.75 * mm});
            skCircle(sketch, "E4.62.0.18", {"center": v(285, -90) * mm, "radius": 0.75 * mm});
            skCircle(sketch, "E4.64.0.18", {"center": v(300, -90) * mm, "radius": 0.75 * mm});
            skCircle(sketch, "E4.66.0.18", {"center": v(315, -90) * mm, "radius": 0.75 * mm});
            skCircle(sketch, "E4.68.0.18", {"center": v(345, -90) * mm, "radius": 0.75 * mm});
            skCircle(sketch, "E4.70.0.18", {"center": v(330, -90) * mm, "radius": 0.75 * mm});
            skCircle(sketch, "E4.0.0.19", {"center": v(-180, -105) * mm, "radius": 0.75 * mm});
            skCircle(sketch, "E4.2.0.19", {"center": v(-165, -105) * mm, "radius": 0.75 * mm});
            skCircle(sketch, "E4.4.0.19", {"center": v(-150, -105) * mm, "radius": 0.75 * mm});
            skCircle(sketch, "E4.6.0.19", {"center": v(-135, -105) * mm, "radius": 0.75 * mm});
            skCircle(sketch, "E4.8.0.19", {"center": v(-120, -105) * mm, "radius": 0.75 * mm});
            skCircle(sketch, "E4.10.0.19", {"center": v(-105, -105) * mm, "radius": 0.75 * mm});
            skCircle(sketch, "E4.12.0.19", {"center": v(-90, -105) * mm, "radius": 0.75 * mm});
            skCircle(sketch, "E4.14.0.19", {"center": v(-75, -105) * mm, "radius": 0.75 * mm});
            skCircle(sketch, "E4.16.0.19", {"center": v(-60, -105) * mm, "radius": 0.75 * mm});
            skCircle(sketch, "E4.18.0.19", {"center": v(-45, -105) * mm, "radius": 0.75 * mm});
            skCircle(sketch, "E4.20.0.19", {"center": v(-30, -105) * mm, "radius": 0.75 * mm});
            skCircle(sketch, "E4.22.0.19", {"center": v(-15, -105) * mm, "radius": 0.75 * mm});
            skCircle(sketch, "E4.24.0.19", {"center": v(0, -105) * mm, "radius": 0.75 * mm});
            skCircle(sketch, "E4.26.0.19", {"center": v(15, -105) * mm, "radius": 0.75 * mm});
            skCircle(sketch, "E4.28.0.19", {"center": v(30, -105) * mm, "radius": 0.75 * mm});
            skCircle(sketch, "E4.30.0.19", {"center": v(45, -105) * mm, "radius": 0.75 * mm});
            skCircle(sketch, "E4.32.0.19", {"center": v(60, -105) * mm, "radius": 0.75 * mm});
            skCircle(sketch, "E4.34.0.19", {"center": v(75, -105) * mm, "radius": 0.75 * mm});
            skCircle(sketch, "E4.36.0.19", {"center": v(90, -105) * mm, "radius": 0.75 * mm});
            skCircle(sketch, "E4.38.0.19", {"center": v(105, -105) * mm, "radius": 0.75 * mm});
            skCircle(sketch, "E4.40.0.19", {"center": v(120, -105) * mm, "radius": 0.75 * mm});
            skCircle(sketch, "E4.42.0.19", {"center": v(135, -105) * mm, "radius": 0.75 * mm});
            skCircle(sketch, "E4.44.0.19", {"center": v(150, -105) * mm, "radius": 0.75 * mm});
            skCircle(sketch, "E4.46.0.19", {"center": v(165, -105) * mm, "radius": 0.75 * mm});
            skCircle(sketch, "E4.48.0.19", {"center": v(180, -105) * mm, "radius": 0.75 * mm});
            skCircle(sketch, "E4.50.0.19", {"center": v(195, -105) * mm, "radius": 0.75 * mm});
            skCircle(sketch, "E4.52.0.19", {"center": v(210, -105) * mm, "radius": 0.75 * mm});
            skCircle(sketch, "E4.54.0.19", {"center": v(225, -105) * mm, "radius": 0.75 * mm});
            skCircle(sketch, "E4.56.0.19", {"center": v(240, -105) * mm, "radius": 0.75 * mm});
            skCircle(sketch, "E4.58.0.19", {"center": v(255, -105) * mm, "radius": 0.75 * mm});
            skCircle(sketch, "E4.60.0.19", {"center": v(270, -105) * mm, "radius": 0.75 * mm});
            skCircle(sketch, "E4.62.0.19", {"center": v(285, -105) * mm, "radius": 0.75 * mm});
            skCircle(sketch, "E4.64.0.19", {"center": v(300, -105) * mm, "radius": 0.75 * mm});
            skCircle(sketch, "E4.66.0.19", {"center": v(315, -105) * mm, "radius": 0.75 * mm});
            skCircle(sketch, "E4.68.0.19", {"center": v(345, -105) * mm, "radius": 0.75 * mm});
            skCircle(sketch, "E4.70.0.19", {"center": v(330, -105) * mm, "radius": 0.75 * mm});
            skCircle(sketch, "E4.0.0.20", {"center": v(-180, -120) * mm, "radius": 0.75 * mm});
            skCircle(sketch, "E4.2.0.20", {"center": v(-165, -120) * mm, "radius": 0.75 * mm});
            skCircle(sketch, "E4.4.0.20", {"center": v(-150, -120) * mm, "radius": 0.75 * mm});
            skCircle(sketch, "E4.6.0.20", {"center": v(-135, -120) * mm, "radius": 0.75 * mm});
            skCircle(sketch, "E4.8.0.20", {"center": v(-120, -120) * mm, "radius": 0.75 * mm});
            skCircle(sketch, "E4.10.0.20", {"center": v(-105, -120) * mm, "radius": 0.75 * mm});
            skCircle(sketch, "E4.12.0.20", {"center": v(-90, -120) * mm, "radius": 0.75 * mm});
            skCircle(sketch, "E4.14.0.20", {"center": v(-75, -120) * mm, "radius": 0.75 * mm});
            skCircle(sketch, "E4.16.0.20", {"center": v(-60, -120) * mm, "radius": 0.75 * mm});
            skCircle(sketch, "E4.18.0.20", {"center": v(-45, -120) * mm, "radius": 0.75 * mm});
            skCircle(sketch, "E4.20.0.20", {"center": v(-30, -120) * mm, "radius": 0.75 * mm});
            skCircle(sketch, "E4.22.0.20", {"center": v(-15, -120) * mm, "radius": 0.75 * mm});
            skCircle(sketch, "E4.24.0.20", {"center": v(0, -120) * mm, "radius": 0.75 * mm});
            skCircle(sketch, "E4.26.0.20", {"center": v(15, -120) * mm, "radius": 0.75 * mm});
            skCircle(sketch, "E4.28.0.20", {"center": v(30, -120) * mm, "radius": 0.75 * mm});
            skCircle(sketch, "E4.30.0.20", {"center": v(45, -120) * mm, "radius": 0.75 * mm});
            skCircle(sketch, "E4.32.0.20", {"center": v(60, -120) * mm, "radius": 0.75 * mm});
            skCircle(sketch, "E4.34.0.20", {"center": v(75, -120) * mm, "radius": 0.75 * mm});
            skCircle(sketch, "E4.36.0.20", {"center": v(90, -120) * mm, "radius": 0.75 * mm});
            skCircle(sketch, "E4.38.0.20", {"center": v(105, -120) * mm, "radius": 0.75 * mm});
            skCircle(sketch, "E4.40.0.20", {"center": v(120, -120) * mm, "radius": 0.75 * mm});
            skCircle(sketch, "E4.42.0.20", {"center": v(135, -120) * mm, "radius": 0.75 * mm});
            skCircle(sketch, "E4.44.0.20", {"center": v(150, -120) * mm, "radius": 0.75 * mm});
            skCircle(sketch, "E4.46.0.20", {"center": v(165, -120) * mm, "radius": 0.75 * mm});
            skCircle(sketch, "E4.48.0.20", {"center": v(180, -120) * mm, "radius": 0.75 * mm});
            skCircle(sketch, "E4.50.0.20", {"center": v(195, -120) * mm, "radius": 0.75 * mm});
            skCircle(sketch, "E4.52.0.20", {"center": v(210, -120) * mm, "radius": 0.75 * mm});
            skCircle(sketch, "E4.54.0.20", {"center": v(225, -120) * mm, "radius": 0.75 * mm});
            skCircle(sketch, "E4.56.0.20", {"center": v(240, -120) * mm, "radius": 0.75 * mm});
            skCircle(sketch, "E4.58.0.20", {"center": v(255, -120) * mm, "radius": 0.75 * mm});
            skCircle(sketch, "E4.60.0.20", {"center": v(270, -120) * mm, "radius": 0.75 * mm});
            skCircle(sketch, "E4.62.0.20", {"center": v(285, -120) * mm, "radius": 0.75 * mm});
            skCircle(sketch, "E4.64.0.20", {"center": v(300, -120) * mm, "radius": 0.75 * mm});
            skCircle(sketch, "E4.66.0.20", {"center": v(315, -120) * mm, "radius": 0.75 * mm});
            skCircle(sketch, "E4.68.0.20", {"center": v(345, -120) * mm, "radius": 0.75 * mm});
            skCircle(sketch, "E4.70.0.20", {"center": v(330, -120) * mm, "radius": 0.75 * mm});
            skCircle(sketch, "E4.0.0.21", {"center": v(-180, -135) * mm, "radius": 0.75 * mm});
            skCircle(sketch, "E4.2.0.21", {"center": v(-165, -135) * mm, "radius": 0.75 * mm});
            skCircle(sketch, "E4.4.0.21", {"center": v(-150, -135) * mm, "radius": 0.75 * mm});
            skCircle(sketch, "E4.6.0.21", {"center": v(-135, -135) * mm, "radius": 0.75 * mm});
            skCircle(sketch, "E4.8.0.21", {"center": v(-120, -135) * mm, "radius": 0.75 * mm});
            skCircle(sketch, "E4.10.0.21", {"center": v(-105, -135) * mm, "radius": 0.75 * mm});
            skCircle(sketch, "E4.12.0.21", {"center": v(-90, -135) * mm, "radius": 0.75 * mm});
            skCircle(sketch, "E4.14.0.21", {"center": v(-75, -135) * mm, "radius": 0.75 * mm});
            skCircle(sketch, "E4.16.0.21", {"center": v(-60, -135) * mm, "radius": 0.75 * mm});
            skCircle(sketch, "E4.18.0.21", {"center": v(-45, -135) * mm, "radius": 0.75 * mm});
            skCircle(sketch, "E4.20.0.21", {"center": v(-30, -135) * mm, "radius": 0.75 * mm});
            skCircle(sketch, "E4.22.0.21", {"center": v(-15, -135) * mm, "radius": 0.75 * mm});
            skCircle(sketch, "E4.24.0.21", {"center": v(0, -135) * mm, "radius": 0.75 * mm});
            skCircle(sketch, "E4.26.0.21", {"center": v(15, -135) * mm, "radius": 0.75 * mm});
            skCircle(sketch, "E4.28.0.21", {"center": v(30, -135) * mm, "radius": 0.75 * mm});
            skCircle(sketch, "E4.30.0.21", {"center": v(45, -135) * mm, "radius": 0.75 * mm});
            skCircle(sketch, "E4.32.0.21", {"center": v(60, -135) * mm, "radius": 0.75 * mm});
            skCircle(sketch, "E4.34.0.21", {"center": v(75, -135) * mm, "radius": 0.75 * mm});
            skCircle(sketch, "E4.36.0.21", {"center": v(90, -135) * mm, "radius": 0.75 * mm});
            skCircle(sketch, "E4.38.0.21", {"center": v(105, -135) * mm, "radius": 0.75 * mm});
            skCircle(sketch, "E4.40.0.21", {"center": v(120, -135) * mm, "radius": 0.75 * mm});
            skCircle(sketch, "E4.42.0.21", {"center": v(135, -135) * mm, "radius": 0.75 * mm});
            skCircle(sketch, "E4.44.0.21", {"center": v(150, -135) * mm, "radius": 0.75 * mm});
            skCircle(sketch, "E4.46.0.21", {"center": v(165, -135) * mm, "radius": 0.75 * mm});
            skCircle(sketch, "E4.48.0.21", {"center": v(180, -135) * mm, "radius": 0.75 * mm});
            skCircle(sketch, "E4.50.0.21", {"center": v(195, -135) * mm, "radius": 0.75 * mm});
            skCircle(sketch, "E4.52.0.21", {"center": v(210, -135) * mm, "radius": 0.75 * mm});
            skCircle(sketch, "E4.54.0.21", {"center": v(225, -135) * mm, "radius": 0.75 * mm});
            skCircle(sketch, "E4.56.0.21", {"center": v(240, -135) * mm, "radius": 0.75 * mm});
            skCircle(sketch, "E4.58.0.21", {"center": v(255, -135) * mm, "radius": 0.75 * mm});
            skCircle(sketch, "E4.60.0.21", {"center": v(270, -135) * mm, "radius": 0.75 * mm});
            skCircle(sketch, "E4.62.0.21", {"center": v(285, -135) * mm, "radius": 0.75 * mm});
            skCircle(sketch, "E4.64.0.21", {"center": v(300, -135) * mm, "radius": 0.75 * mm});
            skCircle(sketch, "E4.66.0.21", {"center": v(315, -135) * mm, "radius": 0.75 * mm});
            skCircle(sketch, "E4.68.0.21", {"center": v(345, -135) * mm, "radius": 0.75 * mm});
            skCircle(sketch, "E4.70.0.21", {"center": v(330, -135) * mm, "radius": 0.75 * mm});
            skCircle(sketch, "E4.0.0.22", {"center": v(-180, -150) * mm, "radius": 0.75 * mm});
            skCircle(sketch, "E4.2.0.22", {"center": v(-165, -150) * mm, "radius": 0.75 * mm});
            skCircle(sketch, "E4.4.0.22", {"center": v(-150, -150) * mm, "radius": 0.75 * mm});
            skCircle(sketch, "E4.6.0.22", {"center": v(-135, -150) * mm, "radius": 0.75 * mm});
            skCircle(sketch, "E4.8.0.22", {"center": v(-120, -150) * mm, "radius": 0.75 * mm});
            skCircle(sketch, "E4.10.0.22", {"center": v(-105, -150) * mm, "radius": 0.75 * mm});
            skCircle(sketch, "E4.12.0.22", {"center": v(-90, -150) * mm, "radius": 0.75 * mm});
            skCircle(sketch, "E4.14.0.22", {"center": v(-75, -150) * mm, "radius": 0.75 * mm});
            skCircle(sketch, "E4.16.0.22", {"center": v(-60, -150) * mm, "radius": 0.75 * mm});
            skCircle(sketch, "E4.18.0.22", {"center": v(-45, -150) * mm, "radius": 0.75 * mm});
            skCircle(sketch, "E4.20.0.22", {"center": v(-30, -150) * mm, "radius": 0.75 * mm});
            skCircle(sketch, "E4.22.0.22", {"center": v(-15, -150) * mm, "radius": 0.75 * mm});
            skCircle(sketch, "E4.24.0.22", {"center": v(0, -150) * mm, "radius": 0.75 * mm});
            skCircle(sketch, "E4.26.0.22", {"center": v(15, -150) * mm, "radius": 0.75 * mm});
            skCircle(sketch, "E4.28.0.22", {"center": v(30, -150) * mm, "radius": 0.75 * mm});
            skCircle(sketch, "E4.30.0.22", {"center": v(45, -150) * mm, "radius": 0.75 * mm});
            skCircle(sketch, "E4.32.0.22", {"center": v(60, -150) * mm, "radius": 0.75 * mm});
            skCircle(sketch, "E4.34.0.22", {"center": v(75, -150) * mm, "radius": 0.75 * mm});
            skCircle(sketch, "E4.36.0.22", {"center": v(90, -150) * mm, "radius": 0.75 * mm});
            skCircle(sketch, "E4.38.0.22", {"center": v(105, -150) * mm, "radius": 0.75 * mm});
            skCircle(sketch, "E4.40.0.22", {"center": v(120, -150) * mm, "radius": 0.75 * mm});
            skCircle(sketch, "E4.42.0.22", {"center": v(135, -150) * mm, "radius": 0.75 * mm});
            skCircle(sketch, "E4.44.0.22", {"center": v(150, -150) * mm, "radius": 0.75 * mm});
            skCircle(sketch, "E4.46.0.22", {"center": v(165, -150) * mm, "radius": 0.75 * mm});
            skCircle(sketch, "E4.48.0.22", {"center": v(180, -150) * mm, "radius": 0.75 * mm});
            skCircle(sketch, "E4.50.0.22", {"center": v(195, -150) * mm, "radius": 0.75 * mm});
            skCircle(sketch, "E4.52.0.22", {"center": v(210, -150) * mm, "radius": 0.75 * mm});
            skCircle(sketch, "E4.54.0.22", {"center": v(225, -150) * mm, "radius": 0.75 * mm});
            skCircle(sketch, "E4.56.0.22", {"center": v(240, -150) * mm, "radius": 0.75 * mm});
            skCircle(sketch, "E4.58.0.22", {"center": v(255, -150) * mm, "radius": 0.75 * mm});
            skCircle(sketch, "E4.60.0.22", {"center": v(270, -150) * mm, "radius": 0.75 * mm});
            skCircle(sketch, "E4.62.0.22", {"center": v(285, -150) * mm, "radius": 0.75 * mm});
            skCircle(sketch, "E4.64.0.22", {"center": v(300, -150) * mm, "radius": 0.75 * mm});
            skCircle(sketch, "E4.66.0.22", {"center": v(315, -150) * mm, "radius": 0.75 * mm});
            skCircle(sketch, "E4.68.0.22", {"center": v(345, -150) * mm, "radius": 0.75 * mm});
            skCircle(sketch, "E4.70.0.22", {"center": v(330, -150) * mm, "radius": 0.75 * mm});
            skCircle(sketch, "E4.0.0.23", {"center": v(-180, -165) * mm, "radius": 0.75 * mm});
            skCircle(sketch, "E4.2.0.23", {"center": v(-165, -165) * mm, "radius": 0.75 * mm});
            skCircle(sketch, "E4.4.0.23", {"center": v(-150, -165) * mm, "radius": 0.75 * mm});
            skCircle(sketch, "E4.6.0.23", {"center": v(-135, -165) * mm, "radius": 0.75 * mm});
            skCircle(sketch, "E4.8.0.23", {"center": v(-120, -165) * mm, "radius": 0.75 * mm});
            skCircle(sketch, "E4.10.0.23", {"center": v(-105, -165) * mm, "radius": 0.75 * mm});
            skCircle(sketch, "E4.12.0.23", {"center": v(-90, -165) * mm, "radius": 0.75 * mm});
            skCircle(sketch, "E4.14.0.23", {"center": v(-75, -165) * mm, "radius": 0.75 * mm});
            skCircle(sketch, "E4.16.0.23", {"center": v(-60, -165) * mm, "radius": 0.75 * mm});
            skCircle(sketch, "E4.18.0.23", {"center": v(-45, -165) * mm, "radius": 0.75 * mm});
            skCircle(sketch, "E4.20.0.23", {"center": v(-30, -165) * mm, "radius": 0.75 * mm});
            skCircle(sketch, "E4.22.0.23", {"center": v(-15, -165) * mm, "radius": 0.75 * mm});
            skCircle(sketch, "E4.24.0.23", {"center": v(0, -165) * mm, "radius": 0.75 * mm});
            skCircle(sketch, "E4.26.0.23", {"center": v(15, -165) * mm, "radius": 0.75 * mm});
            skCircle(sketch, "E4.28.0.23", {"center": v(30, -165) * mm, "radius": 0.75 * mm});
            skCircle(sketch, "E4.30.0.23", {"center": v(45, -165) * mm, "radius": 0.75 * mm});
            skCircle(sketch, "E4.32.0.23", {"center": v(60, -165) * mm, "radius": 0.75 * mm});
            skCircle(sketch, "E4.34.0.23", {"center": v(75, -165) * mm, "radius": 0.75 * mm});
            skCircle(sketch, "E4.36.0.23", {"center": v(90, -165) * mm, "radius": 0.75 * mm});
            skCircle(sketch, "E4.38.0.23", {"center": v(105, -165) * mm, "radius": 0.75 * mm});
            skCircle(sketch, "E4.40.0.23", {"center": v(120, -165) * mm, "radius": 0.75 * mm});
            skCircle(sketch, "E4.42.0.23", {"center": v(135, -165) * mm, "radius": 0.75 * mm});
            skCircle(sketch, "E4.44.0.23", {"center": v(150, -165) * mm, "radius": 0.75 * mm});
            skCircle(sketch, "E4.46.0.23", {"center": v(165, -165) * mm, "radius": 0.75 * mm});
            skCircle(sketch, "E4.48.0.23", {"center": v(180, -165) * mm, "radius": 0.75 * mm});
            skCircle(sketch, "E4.50.0.23", {"center": v(195, -165) * mm, "radius": 0.75 * mm});
            skCircle(sketch, "E4.52.0.23", {"center": v(210, -165) * mm, "radius": 0.75 * mm});
            skCircle(sketch, "E4.54.0.23", {"center": v(225, -165) * mm, "radius": 0.75 * mm});
            skCircle(sketch, "E4.56.0.23", {"center": v(240, -165) * mm, "radius": 0.75 * mm});
            skCircle(sketch, "E4.58.0.23", {"center": v(255, -165) * mm, "radius": 0.75 * mm});
            skCircle(sketch, "E4.60.0.23", {"center": v(270, -165) * mm, "radius": 0.75 * mm});
            skCircle(sketch, "E4.62.0.23", {"center": v(285, -165) * mm, "radius": 0.75 * mm});
            skCircle(sketch, "E4.64.0.23", {"center": v(300, -165) * mm, "radius": 0.75 * mm});
            skCircle(sketch, "E4.66.0.23", {"center": v(315, -165) * mm, "radius": 0.75 * mm});
            skCircle(sketch, "E4.68.0.23", {"center": v(345, -165) * mm, "radius": 0.75 * mm});
            skCircle(sketch, "E4.70.0.23", {"center": v(330, -165) * mm, "radius": 0.75 * mm});
            skCircle(sketch, "E4.0.0.24", {"center": v(-180, -180) * mm, "radius": 0.75 * mm});
            skCircle(sketch, "E4.2.0.24", {"center": v(-165, -180) * mm, "radius": 0.75 * mm});
            skCircle(sketch, "E4.4.0.24", {"center": v(-150, -180) * mm, "radius": 0.75 * mm});
            skCircle(sketch, "E4.6.0.24", {"center": v(-135, -180) * mm, "radius": 0.75 * mm});
            skCircle(sketch, "E4.8.0.24", {"center": v(-120, -180) * mm, "radius": 0.75 * mm});
            skCircle(sketch, "E4.10.0.24", {"center": v(-105, -180) * mm, "radius": 0.75 * mm});
            skCircle(sketch, "E4.12.0.24", {"center": v(-90, -180) * mm, "radius": 0.75 * mm});
            skCircle(sketch, "E4.14.0.24", {"center": v(-75, -180) * mm, "radius": 0.75 * mm});
            skCircle(sketch, "E4.16.0.24", {"center": v(-60, -180) * mm, "radius": 0.75 * mm});
            skCircle(sketch, "E4.18.0.24", {"center": v(-45, -180) * mm, "radius": 0.75 * mm});
            skCircle(sketch, "E4.20.0.24", {"center": v(-30, -180) * mm, "radius": 0.75 * mm});
            skCircle(sketch, "E4.22.0.24", {"center": v(-15, -180) * mm, "radius": 0.75 * mm});
            skCircle(sketch, "E4.24.0.24", {"center": v(0, -180) * mm, "radius": 0.75 * mm});
            skCircle(sketch, "E4.26.0.24", {"center": v(15, -180) * mm, "radius": 0.75 * mm});
            skCircle(sketch, "E4.28.0.24", {"center": v(30, -180) * mm, "radius": 0.75 * mm});
            skCircle(sketch, "E4.30.0.24", {"center": v(45, -180) * mm, "radius": 0.75 * mm});
            skCircle(sketch, "E4.32.0.24", {"center": v(60, -180) * mm, "radius": 0.75 * mm});
            skCircle(sketch, "E4.34.0.24", {"center": v(75, -180) * mm, "radius": 0.75 * mm});
            skCircle(sketch, "E4.36.0.24", {"center": v(90, -180) * mm, "radius": 0.75 * mm});
            skCircle(sketch, "E4.38.0.24", {"center": v(105, -180) * mm, "radius": 0.75 * mm});
            skCircle(sketch, "E4.40.0.24", {"center": v(120, -180) * mm, "radius": 0.75 * mm});
            skCircle(sketch, "E4.42.0.24", {"center": v(135, -180) * mm, "radius": 0.75 * mm});
            skCircle(sketch, "E4.44.0.24", {"center": v(150, -180) * mm, "radius": 0.75 * mm});
            skCircle(sketch, "E4.46.0.24", {"center": v(165, -180) * mm, "radius": 0.75 * mm});
            skCircle(sketch, "E4.48.0.24", {"center": v(180, -180) * mm, "radius": 0.75 * mm});
            skCircle(sketch, "E4.50.0.24", {"center": v(195, -180) * mm, "radius": 0.75 * mm});
            skCircle(sketch, "E4.52.0.24", {"center": v(210, -180) * mm, "radius": 0.75 * mm});
            skCircle(sketch, "E4.54.0.24", {"center": v(225, -180) * mm, "radius": 0.75 * mm});
            skCircle(sketch, "E4.56.0.24", {"center": v(240, -180) * mm, "radius": 0.75 * mm});
            skCircle(sketch, "E4.58.0.24", {"center": v(255, -180) * mm, "radius": 0.75 * mm});
            skCircle(sketch, "E4.60.0.24", {"center": v(270, -180) * mm, "radius": 0.75 * mm});
            skCircle(sketch, "E4.62.0.24", {"center": v(285, -180) * mm, "radius": 0.75 * mm});
            skCircle(sketch, "E4.64.0.24", {"center": v(300, -180) * mm, "radius": 0.75 * mm});
            skCircle(sketch, "E4.66.0.24", {"center": v(315, -180) * mm, "radius": 0.75 * mm});
            skCircle(sketch, "E4.68.0.24", {"center": v(345, -180) * mm, "radius": 0.75 * mm});
            skCircle(sketch, "E4.70.0.24", {"center": v(330, -180) * mm, "radius": 0.75 * mm});
            skCircle(sketch, "E4.0.0.25", {"center": v(-180, -195) * mm, "radius": 0.75 * mm});
            skCircle(sketch, "E4.2.0.25", {"center": v(-165, -195) * mm, "radius": 0.75 * mm});
            skCircle(sketch, "E4.4.0.25", {"center": v(-150, -195) * mm, "radius": 0.75 * mm});
            skCircle(sketch, "E4.6.0.25", {"center": v(-135, -195) * mm, "radius": 0.75 * mm});
            skCircle(sketch, "E4.8.0.25", {"center": v(-120, -195) * mm, "radius": 0.75 * mm});
            skCircle(sketch, "E4.10.0.25", {"center": v(-105, -195) * mm, "radius": 0.75 * mm});
            skCircle(sketch, "E4.12.0.25", {"center": v(-90, -195) * mm, "radius": 0.75 * mm});
            skCircle(sketch, "E4.14.0.25", {"center": v(-75, -195) * mm, "radius": 0.75 * mm});
            skCircle(sketch, "E4.16.0.25", {"center": v(-60, -195) * mm, "radius": 0.75 * mm});
            skCircle(sketch, "E4.18.0.25", {"center": v(-45, -195) * mm, "radius": 0.75 * mm});
            skCircle(sketch, "E4.20.0.25", {"center": v(-30, -195) * mm, "radius": 0.75 * mm});
            skCircle(sketch, "E4.22.0.25", {"center": v(-15, -195) * mm, "radius": 0.75 * mm});
            skCircle(sketch, "E4.24.0.25", {"center": v(0, -195) * mm, "radius": 0.75 * mm});
            skCircle(sketch, "E4.26.0.25", {"center": v(15, -195) * mm, "radius": 0.75 * mm});
            skCircle(sketch, "E4.28.0.25", {"center": v(30, -195) * mm, "radius": 0.75 * mm});
            skCircle(sketch, "E4.30.0.25", {"center": v(45, -195) * mm, "radius": 0.75 * mm});
            skCircle(sketch, "E4.32.0.25", {"center": v(60, -195) * mm, "radius": 0.75 * mm});
            skCircle(sketch, "E4.34.0.25", {"center": v(75, -195) * mm, "radius": 0.75 * mm});
            skCircle(sketch, "E4.36.0.25", {"center": v(90, -195) * mm, "radius": 0.75 * mm});
            skCircle(sketch, "E4.38.0.25", {"center": v(105, -195) * mm, "radius": 0.75 * mm});
            skCircle(sketch, "E4.40.0.25", {"center": v(120, -195) * mm, "radius": 0.75 * mm});
            skCircle(sketch, "E4.42.0.25", {"center": v(135, -195) * mm, "radius": 0.75 * mm});
            skCircle(sketch, "E4.44.0.25", {"center": v(150, -195) * mm, "radius": 0.75 * mm});
            skCircle(sketch, "E4.46.0.25", {"center": v(165, -195) * mm, "radius": 0.75 * mm});
            skCircle(sketch, "E4.48.0.25", {"center": v(180, -195) * mm, "radius": 0.75 * mm});
            skCircle(sketch, "E4.50.0.25", {"center": v(195, -195) * mm, "radius": 0.75 * mm});
            skCircle(sketch, "E4.52.0.25", {"center": v(210, -195) * mm, "radius": 0.75 * mm});
            skCircle(sketch, "E4.54.0.25", {"center": v(225, -195) * mm, "radius": 0.75 * mm});
            skCircle(sketch, "E4.56.0.25", {"center": v(240, -195) * mm, "radius": 0.75 * mm});
            skCircle(sketch, "E4.58.0.25", {"center": v(255, -195) * mm, "radius": 0.75 * mm});
            skCircle(sketch, "E4.60.0.25", {"center": v(270, -195) * mm, "radius": 0.75 * mm});
            skCircle(sketch, "E4.62.0.25", {"center": v(285, -195) * mm, "radius": 0.75 * mm});
            skCircle(sketch, "E4.64.0.25", {"center": v(300, -195) * mm, "radius": 0.75 * mm});
            skCircle(sketch, "E4.66.0.25", {"center": v(315, -195) * mm, "radius": 0.75 * mm});
            skCircle(sketch, "E4.68.0.25", {"center": v(345, -195) * mm, "radius": 0.75 * mm});
            skCircle(sketch, "E4.70.0.25", {"center": v(330, -195) * mm, "radius": 0.75 * mm});
            skCircle(sketch, "E4.0.0.26", {"center": v(-180, -210) * mm, "radius": 0.75 * mm});
            skCircle(sketch, "E4.2.0.26", {"center": v(-165, -210) * mm, "radius": 0.75 * mm});
            skCircle(sketch, "E4.4.0.26", {"center": v(-150, -210) * mm, "radius": 0.75 * mm});
            skCircle(sketch, "E4.6.0.26", {"center": v(-135, -210) * mm, "radius": 0.75 * mm});
            skCircle(sketch, "E4.8.0.26", {"center": v(-120, -210) * mm, "radius": 0.75 * mm});
            skCircle(sketch, "E4.10.0.26", {"center": v(-105, -210) * mm, "radius": 0.75 * mm});
            skCircle(sketch, "E4.12.0.26", {"center": v(-90, -210) * mm, "radius": 0.75 * mm});
            skCircle(sketch, "E4.14.0.26", {"center": v(-75, -210) * mm, "radius": 0.75 * mm});
            skCircle(sketch, "E4.16.0.26", {"center": v(-60, -210) * mm, "radius": 0.75 * mm});
            skCircle(sketch, "E4.18.0.26", {"center": v(-45, -210) * mm, "radius": 0.75 * mm});
            skCircle(sketch, "E4.20.0.26", {"center": v(-30, -210) * mm, "radius": 0.75 * mm});
            skCircle(sketch, "E4.22.0.26", {"center": v(-15, -210) * mm, "radius": 0.75 * mm});
            skCircle(sketch, "E4.24.0.26", {"center": v(0, -210) * mm, "radius": 0.75 * mm});
            skCircle(sketch, "E4.26.0.26", {"center": v(15, -210) * mm, "radius": 0.75 * mm});
            skCircle(sketch, "E4.28.0.26", {"center": v(30, -210) * mm, "radius": 0.75 * mm});
            skCircle(sketch, "E4.30.0.26", {"center": v(45, -210) * mm, "radius": 0.75 * mm});
            skCircle(sketch, "E4.32.0.26", {"center": v(60, -210) * mm, "radius": 0.75 * mm});
            skCircle(sketch, "E4.34.0.26", {"center": v(75, -210) * mm, "radius": 0.75 * mm});
            skCircle(sketch, "E4.36.0.26", {"center": v(90, -210) * mm, "radius": 0.75 * mm});
            skCircle(sketch, "E4.38.0.26", {"center": v(105, -210) * mm, "radius": 0.75 * mm});
            skCircle(sketch, "E4.40.0.26", {"center": v(120, -210) * mm, "radius": 0.75 * mm});
            skCircle(sketch, "E4.42.0.26", {"center": v(135, -210) * mm, "radius": 0.75 * mm});
            skCircle(sketch, "E4.44.0.26", {"center": v(150, -210) * mm, "radius": 0.75 * mm});
            skCircle(sketch, "E4.46.0.26", {"center": v(165, -210) * mm, "radius": 0.75 * mm});
            skCircle(sketch, "E4.48.0.26", {"center": v(180, -210) * mm, "radius": 0.75 * mm});
            skCircle(sketch, "E4.50.0.26", {"center": v(195, -210) * mm, "radius": 0.75 * mm});
            skCircle(sketch, "E4.52.0.26", {"center": v(210, -210) * mm, "radius": 0.75 * mm});
            skCircle(sketch, "E4.54.0.26", {"center": v(225, -210) * mm, "radius": 0.75 * mm});
            skCircle(sketch, "E4.56.0.26", {"center": v(240, -210) * mm, "radius": 0.75 * mm});
            skCircle(sketch, "E4.58.0.26", {"center": v(255, -210) * mm, "radius": 0.75 * mm});
            skCircle(sketch, "E4.60.0.26", {"center": v(270, -210) * mm, "radius": 0.75 * mm});
            skCircle(sketch, "E4.62.0.26", {"center": v(285, -210) * mm, "radius": 0.75 * mm});
            skCircle(sketch, "E4.64.0.26", {"center": v(300, -210) * mm, "radius": 0.75 * mm});
            skCircle(sketch, "E4.66.0.26", {"center": v(315, -210) * mm, "radius": 0.75 * mm});
            skCircle(sketch, "E4.68.0.26", {"center": v(345, -210) * mm, "radius": 0.75 * mm});
            skCircle(sketch, "E4.70.0.26", {"center": v(330, -210) * mm, "radius": 0.75 * mm});
            skCircle(sketch, "E4.0.0.27", {"center": v(-180, -225) * mm, "radius": 0.75 * mm});
            skCircle(sketch, "E4.2.0.27", {"center": v(-165, -225) * mm, "radius": 0.75 * mm});
            skCircle(sketch, "E4.4.0.27", {"center": v(-150, -225) * mm, "radius": 0.75 * mm});
            skCircle(sketch, "E4.6.0.27", {"center": v(-135, -225) * mm, "radius": 0.75 * mm});
            skCircle(sketch, "E4.8.0.27", {"center": v(-120, -225) * mm, "radius": 0.75 * mm});
            skCircle(sketch, "E4.10.0.27", {"center": v(-105, -225) * mm, "radius": 0.75 * mm});
            skCircle(sketch, "E4.12.0.27", {"center": v(-90, -225) * mm, "radius": 0.75 * mm});
            skCircle(sketch, "E4.14.0.27", {"center": v(-75, -225) * mm, "radius": 0.75 * mm});
            skCircle(sketch, "E4.16.0.27", {"center": v(-60, -225) * mm, "radius": 0.75 * mm});
            skCircle(sketch, "E4.18.0.27", {"center": v(-45, -225) * mm, "radius": 0.75 * mm});
            skCircle(sketch, "E4.20.0.27", {"center": v(-30, -225) * mm, "radius": 0.75 * mm});
            skCircle(sketch, "E4.22.0.27", {"center": v(-15, -225) * mm, "radius": 0.75 * mm});
            skCircle(sketch, "E4.24.0.27", {"center": v(0, -225) * mm, "radius": 0.75 * mm});
            skCircle(sketch, "E4.26.0.27", {"center": v(15, -225) * mm, "radius": 0.75 * mm});
            skCircle(sketch, "E4.28.0.27", {"center": v(30, -225) * mm, "radius": 0.75 * mm});
            skCircle(sketch, "E4.30.0.27", {"center": v(45, -225) * mm, "radius": 0.75 * mm});
            skCircle(sketch, "E4.32.0.27", {"center": v(60, -225) * mm, "radius": 0.75 * mm});
            skCircle(sketch, "E4.34.0.27", {"center": v(75, -225) * mm, "radius": 0.75 * mm});
            skCircle(sketch, "E4.36.0.27", {"center": v(90, -225) * mm, "radius": 0.75 * mm});
            skCircle(sketch, "E4.38.0.27", {"center": v(105, -225) * mm, "radius": 0.75 * mm});
            skCircle(sketch, "E4.40.0.27", {"center": v(120, -225) * mm, "radius": 0.75 * mm});
            skCircle(sketch, "E4.42.0.27", {"center": v(135, -225) * mm, "radius": 0.75 * mm});
            skCircle(sketch, "E4.44.0.27", {"center": v(150, -225) * mm, "radius": 0.75 * mm});
            skCircle(sketch, "E4.46.0.27", {"center": v(165, -225) * mm, "radius": 0.75 * mm});
            skCircle(sketch, "E4.48.0.27", {"center": v(180, -225) * mm, "radius": 0.75 * mm});
            skCircle(sketch, "E4.50.0.27", {"center": v(195, -225) * mm, "radius": 0.75 * mm});
            skCircle(sketch, "E4.52.0.27", {"center": v(210, -225) * mm, "radius": 0.75 * mm});
            skCircle(sketch, "E4.54.0.27", {"center": v(225, -225) * mm, "radius": 0.75 * mm});
            skCircle(sketch, "E4.56.0.27", {"center": v(240, -225) * mm, "radius": 0.75 * mm});
            skCircle(sketch, "E4.58.0.27", {"center": v(255, -225) * mm, "radius": 0.75 * mm});
            skCircle(sketch, "E4.60.0.27", {"center": v(270, -225) * mm, "radius": 0.75 * mm});
            skCircle(sketch, "E4.62.0.27", {"center": v(285, -225) * mm, "radius": 0.75 * mm});
            skCircle(sketch, "E4.64.0.27", {"center": v(300, -225) * mm, "radius": 0.75 * mm});
            skCircle(sketch, "E4.66.0.27", {"center": v(315, -225) * mm, "radius": 0.75 * mm});
            skCircle(sketch, "E4.68.0.27", {"center": v(345, -225) * mm, "radius": 0.75 * mm});
            skCircle(sketch, "E4.70.0.27", {"center": v(330, -225) * mm, "radius": 0.75 * mm});
            skCircle(sketch, "E4.0.0.28", {"center": v(-180, -240) * mm, "radius": 0.75 * mm});
            skCircle(sketch, "E4.2.0.28", {"center": v(-165, -240) * mm, "radius": 0.75 * mm});
            skCircle(sketch, "E4.4.0.28", {"center": v(-150, -240) * mm, "radius": 0.75 * mm});
            skCircle(sketch, "E4.6.0.28", {"center": v(-135, -240) * mm, "radius": 0.75 * mm});
            skCircle(sketch, "E4.8.0.28", {"center": v(-120, -240) * mm, "radius": 0.75 * mm});
            skCircle(sketch, "E4.10.0.28", {"center": v(-105, -240) * mm, "radius": 0.75 * mm});
            skCircle(sketch, "E4.12.0.28", {"center": v(-90, -240) * mm, "radius": 0.75 * mm});
            skCircle(sketch, "E4.14.0.28", {"center": v(-75, -240) * mm, "radius": 0.75 * mm});
            skCircle(sketch, "E4.16.0.28", {"center": v(-60, -240) * mm, "radius": 0.75 * mm});
            skCircle(sketch, "E4.18.0.28", {"center": v(-45, -240) * mm, "radius": 0.75 * mm});
            skCircle(sketch, "E4.20.0.28", {"center": v(-30, -240) * mm, "radius": 0.75 * mm});
            skCircle(sketch, "E4.22.0.28", {"center": v(-15, -240) * mm, "radius": 0.75 * mm});
            skCircle(sketch, "E4.24.0.28", {"center": v(0, -240) * mm, "radius": 0.75 * mm});
            skCircle(sketch, "E4.26.0.28", {"center": v(15, -240) * mm, "radius": 0.75 * mm});
            skCircle(sketch, "E4.28.0.28", {"center": v(30, -240) * mm, "radius": 0.75 * mm});
            skCircle(sketch, "E4.30.0.28", {"center": v(45, -240) * mm, "radius": 0.75 * mm});
            skCircle(sketch, "E4.32.0.28", {"center": v(60, -240) * mm, "radius": 0.75 * mm});
            skCircle(sketch, "E4.34.0.28", {"center": v(75, -240) * mm, "radius": 0.75 * mm});
            skCircle(sketch, "E4.36.0.28", {"center": v(90, -240) * mm, "radius": 0.75 * mm});
            skCircle(sketch, "E4.38.0.28", {"center": v(105, -240) * mm, "radius": 0.75 * mm});
            skCircle(sketch, "E4.40.0.28", {"center": v(120, -240) * mm, "radius": 0.75 * mm});
            skCircle(sketch, "E4.42.0.28", {"center": v(135, -240) * mm, "radius": 0.75 * mm});
            skCircle(sketch, "E4.44.0.28", {"center": v(150, -240) * mm, "radius": 0.75 * mm});
            skCircle(sketch, "E4.46.0.28", {"center": v(165, -240) * mm, "radius": 0.75 * mm});
            skCircle(sketch, "E4.48.0.28", {"center": v(180, -240) * mm, "radius": 0.75 * mm});
            skCircle(sketch, "E4.50.0.28", {"center": v(195, -240) * mm, "radius": 0.75 * mm});
            skCircle(sketch, "E4.52.0.28", {"center": v(210, -240) * mm, "radius": 0.75 * mm});
            skCircle(sketch, "E4.54.0.28", {"center": v(225, -240) * mm, "radius": 0.75 * mm});
            skCircle(sketch, "E4.56.0.28", {"center": v(240, -240) * mm, "radius": 0.75 * mm});
            skCircle(sketch, "E4.58.0.28", {"center": v(255, -240) * mm, "radius": 0.75 * mm});
            skCircle(sketch, "E4.60.0.28", {"center": v(270, -240) * mm, "radius": 0.75 * mm});
            skCircle(sketch, "E4.62.0.28", {"center": v(285, -240) * mm, "radius": 0.75 * mm});
            skCircle(sketch, "E4.64.0.28", {"center": v(300, -240) * mm, "radius": 0.75 * mm});
            skCircle(sketch, "E4.66.0.28", {"center": v(315, -240) * mm, "radius": 0.75 * mm});
            skCircle(sketch, "E4.68.0.28", {"center": v(345, -240) * mm, "radius": 0.75 * mm});
            skCircle(sketch, "E4.70.0.28", {"center": v(330, -240) * mm, "radius": 0.75 * mm});
            skCircle(sketch, "E4.0.0.29", {"center": v(-180, -255) * mm, "radius": 0.75 * mm});
            skCircle(sketch, "E4.2.0.29", {"center": v(-165, -255) * mm, "radius": 0.75 * mm});
            skCircle(sketch, "E4.4.0.29", {"center": v(-150, -255) * mm, "radius": 0.75 * mm});
            skCircle(sketch, "E4.6.0.29", {"center": v(-135, -255) * mm, "radius": 0.75 * mm});
            skCircle(sketch, "E4.8.0.29", {"center": v(-120, -255) * mm, "radius": 0.75 * mm});
            skCircle(sketch, "E4.10.0.29", {"center": v(-105, -255) * mm, "radius": 0.75 * mm});
            skCircle(sketch, "E4.12.0.29", {"center": v(-90, -255) * mm, "radius": 0.75 * mm});
            skCircle(sketch, "E4.14.0.29", {"center": v(-75, -255) * mm, "radius": 0.75 * mm});
            skCircle(sketch, "E4.16.0.29", {"center": v(-60, -255) * mm, "radius": 0.75 * mm});
            skCircle(sketch, "E4.18.0.29", {"center": v(-45, -255) * mm, "radius": 0.75 * mm});
            skCircle(sketch, "E4.20.0.29", {"center": v(-30, -255) * mm, "radius": 0.75 * mm});
            skCircle(sketch, "E4.22.0.29", {"center": v(-15, -255) * mm, "radius": 0.75 * mm});
            skCircle(sketch, "E4.24.0.29", {"center": v(0, -255) * mm, "radius": 0.75 * mm});
            skCircle(sketch, "E4.26.0.29", {"center": v(15, -255) * mm, "radius": 0.75 * mm});
            skCircle(sketch, "E4.28.0.29", {"center": v(30, -255) * mm, "radius": 0.75 * mm});
            skCircle(sketch, "E4.30.0.29", {"center": v(45, -255) * mm, "radius": 0.75 * mm});
            skCircle(sketch, "E4.32.0.29", {"center": v(60, -255) * mm, "radius": 0.75 * mm});
            skCircle(sketch, "E4.34.0.29", {"center": v(75, -255) * mm, "radius": 0.75 * mm});
            skCircle(sketch, "E4.36.0.29", {"center": v(90, -255) * mm, "radius": 0.75 * mm});
            skCircle(sketch, "E4.38.0.29", {"center": v(105, -255) * mm, "radius": 0.75 * mm});
            skCircle(sketch, "E4.40.0.29", {"center": v(120, -255) * mm, "radius": 0.75 * mm});
            skCircle(sketch, "E4.42.0.29", {"center": v(135, -255) * mm, "radius": 0.75 * mm});
            skCircle(sketch, "E4.44.0.29", {"center": v(150, -255) * mm, "radius": 0.75 * mm});
            skCircle(sketch, "E4.46.0.29", {"center": v(165, -255) * mm, "radius": 0.75 * mm});
            skCircle(sketch, "E4.48.0.29", {"center": v(180, -255) * mm, "radius": 0.75 * mm});
            skCircle(sketch, "E4.50.0.29", {"center": v(195, -255) * mm, "radius": 0.75 * mm});
            skCircle(sketch, "E4.52.0.29", {"center": v(210, -255) * mm, "radius": 0.75 * mm});
            skCircle(sketch, "E4.54.0.29", {"center": v(225, -255) * mm, "radius": 0.75 * mm});
            skCircle(sketch, "E4.56.0.29", {"center": v(240, -255) * mm, "radius": 0.75 * mm});
            skCircle(sketch, "E4.58.0.29", {"center": v(255, -255) * mm, "radius": 0.75 * mm});
            skCircle(sketch, "E4.60.0.29", {"center": v(270, -255) * mm, "radius": 0.75 * mm});
            skCircle(sketch, "E4.62.0.29", {"center": v(285, -255) * mm, "radius": 0.75 * mm});
            skCircle(sketch, "E4.64.0.29", {"center": v(300, -255) * mm, "radius": 0.75 * mm});
            skCircle(sketch, "E4.66.0.29", {"center": v(315, -255) * mm, "radius": 0.75 * mm});
            skCircle(sketch, "E4.68.0.29", {"center": v(345, -255) * mm, "radius": 0.75 * mm});
            skCircle(sketch, "E4.70.0.29", {"center": v(330, -255) * mm, "radius": 0.75 * mm});
            skCircle(sketch, "E4.0.0.30", {"center": v(-180, -270) * mm, "radius": 0.75 * mm});
            skCircle(sketch, "E4.2.0.30", {"center": v(-165, -270) * mm, "radius": 0.75 * mm});
            skCircle(sketch, "E4.4.0.30", {"center": v(-150, -270) * mm, "radius": 0.75 * mm});
            skCircle(sketch, "E4.6.0.30", {"center": v(-135, -270) * mm, "radius": 0.75 * mm});
            skCircle(sketch, "E4.8.0.30", {"center": v(-120, -270) * mm, "radius": 0.75 * mm});
            skCircle(sketch, "E4.10.0.30", {"center": v(-105, -270) * mm, "radius": 0.75 * mm});
            skCircle(sketch, "E4.12.0.30", {"center": v(-90, -270) * mm, "radius": 0.75 * mm});
            skCircle(sketch, "E4.14.0.30", {"center": v(-75, -270) * mm, "radius": 0.75 * mm});
            skCircle(sketch, "E4.16.0.30", {"center": v(-60, -270) * mm, "radius": 0.75 * mm});
            skCircle(sketch, "E4.18.0.30", {"center": v(-45, -270) * mm, "radius": 0.75 * mm});
            skCircle(sketch, "E4.20.0.30", {"center": v(-30, -270) * mm, "radius": 0.75 * mm});
            skCircle(sketch, "E4.22.0.30", {"center": v(-15, -270) * mm, "radius": 0.75 * mm});
            skCircle(sketch, "E4.24.0.30", {"center": v(0, -270) * mm, "radius": 0.75 * mm});
            skCircle(sketch, "E4.26.0.30", {"center": v(15, -270) * mm, "radius": 0.75 * mm});
            skCircle(sketch, "E4.28.0.30", {"center": v(30, -270) * mm, "radius": 0.75 * mm});
            skCircle(sketch, "E4.30.0.30", {"center": v(45, -270) * mm, "radius": 0.75 * mm});
            skCircle(sketch, "E4.32.0.30", {"center": v(60, -270) * mm, "radius": 0.75 * mm});
            skCircle(sketch, "E4.34.0.30", {"center": v(75, -270) * mm, "radius": 0.75 * mm});
            skCircle(sketch, "E4.36.0.30", {"center": v(90, -270) * mm, "radius": 0.75 * mm});
            skCircle(sketch, "E4.38.0.30", {"center": v(105, -270) * mm, "radius": 0.75 * mm});
            skCircle(sketch, "E4.40.0.30", {"center": v(120, -270) * mm, "radius": 0.75 * mm});
            skCircle(sketch, "E4.42.0.30", {"center": v(135, -270) * mm, "radius": 0.75 * mm});
            skCircle(sketch, "E4.44.0.30", {"center": v(150, -270) * mm, "radius": 0.75 * mm});
            skCircle(sketch, "E4.46.0.30", {"center": v(165, -270) * mm, "radius": 0.75 * mm});
            skCircle(sketch, "E4.48.0.30", {"center": v(180, -270) * mm, "radius": 0.75 * mm});
            skCircle(sketch, "E4.50.0.30", {"center": v(195, -270) * mm, "radius": 0.75 * mm});
            skCircle(sketch, "E4.52.0.30", {"center": v(210, -270) * mm, "radius": 0.75 * mm});
            skCircle(sketch, "E4.54.0.30", {"center": v(225, -270) * mm, "radius": 0.75 * mm});
            skCircle(sketch, "E4.56.0.30", {"center": v(240, -270) * mm, "radius": 0.75 * mm});
            skCircle(sketch, "E4.58.0.30", {"center": v(255, -270) * mm, "radius": 0.75 * mm});
            skCircle(sketch, "E4.60.0.30", {"center": v(270, -270) * mm, "radius": 0.75 * mm});
            skCircle(sketch, "E4.62.0.30", {"center": v(285, -270) * mm, "radius": 0.75 * mm});
            skCircle(sketch, "E4.64.0.30", {"center": v(300, -270) * mm, "radius": 0.75 * mm});
            skCircle(sketch, "E4.66.0.30", {"center": v(315, -270) * mm, "radius": 0.75 * mm});
            skCircle(sketch, "E4.68.0.30", {"center": v(345, -270) * mm, "radius": 0.75 * mm});
            skCircle(sketch, "E4.70.0.30", {"center": v(330, -270) * mm, "radius": 0.75 * mm});
            skCircle(sketch, "E4.0.0.31", {"center": v(-180, -285) * mm, "radius": 0.75 * mm});
            skCircle(sketch, "E4.2.0.31", {"center": v(-165, -285) * mm, "radius": 0.75 * mm});
            skCircle(sketch, "E4.4.0.31", {"center": v(-150, -285) * mm, "radius": 0.75 * mm});
            skCircle(sketch, "E4.6.0.31", {"center": v(-135, -285) * mm, "radius": 0.75 * mm});
            skCircle(sketch, "E4.8.0.31", {"center": v(-120, -285) * mm, "radius": 0.75 * mm});
            skCircle(sketch, "E4.10.0.31", {"center": v(-105, -285) * mm, "radius": 0.75 * mm});
            skCircle(sketch, "E4.12.0.31", {"center": v(-90, -285) * mm, "radius": 0.75 * mm});
            skCircle(sketch, "E4.14.0.31", {"center": v(-75, -285) * mm, "radius": 0.75 * mm});
            skCircle(sketch, "E4.16.0.31", {"center": v(-60, -285) * mm, "radius": 0.75 * mm});
            skCircle(sketch, "E4.18.0.31", {"center": v(-45, -285) * mm, "radius": 0.75 * mm});
            skCircle(sketch, "E4.20.0.31", {"center": v(-30, -285) * mm, "radius": 0.75 * mm});
            skCircle(sketch, "E4.22.0.31", {"center": v(-15, -285) * mm, "radius": 0.75 * mm});
            skCircle(sketch, "E4.24.0.31", {"center": v(0, -285) * mm, "radius": 0.75 * mm});
            skCircle(sketch, "E4.26.0.31", {"center": v(15, -285) * mm, "radius": 0.75 * mm});
            skCircle(sketch, "E4.28.0.31", {"center": v(30, -285) * mm, "radius": 0.75 * mm});
            skCircle(sketch, "E4.30.0.31", {"center": v(45, -285) * mm, "radius": 0.75 * mm});
            skCircle(sketch, "E4.32.0.31", {"center": v(60, -285) * mm, "radius": 0.75 * mm});
            skCircle(sketch, "E4.34.0.31", {"center": v(75, -285) * mm, "radius": 0.75 * mm});
            skCircle(sketch, "E4.36.0.31", {"center": v(90, -285) * mm, "radius": 0.75 * mm});
            skCircle(sketch, "E4.38.0.31", {"center": v(105, -285) * mm, "radius": 0.75 * mm});
            skCircle(sketch, "E4.40.0.31", {"center": v(120, -285) * mm, "radius": 0.75 * mm});
            skCircle(sketch, "E4.42.0.31", {"center": v(135, -285) * mm, "radius": 0.75 * mm});
            skCircle(sketch, "E4.44.0.31", {"center": v(150, -285) * mm, "radius": 0.75 * mm});
            skCircle(sketch, "E4.46.0.31", {"center": v(165, -285) * mm, "radius": 0.75 * mm});
            skCircle(sketch, "E4.48.0.31", {"center": v(180, -285) * mm, "radius": 0.75 * mm});
            skCircle(sketch, "E4.50.0.31", {"center": v(195, -285) * mm, "radius": 0.75 * mm});
            skCircle(sketch, "E4.52.0.31", {"center": v(210, -285) * mm, "radius": 0.75 * mm});
            skCircle(sketch, "E4.54.0.31", {"center": v(225, -285) * mm, "radius": 0.75 * mm});
            skCircle(sketch, "E4.56.0.31", {"center": v(240, -285) * mm, "radius": 0.75 * mm});
            skCircle(sketch, "E4.58.0.31", {"center": v(255, -285) * mm, "radius": 0.75 * mm});
            skCircle(sketch, "E4.60.0.31", {"center": v(270, -285) * mm, "radius": 0.75 * mm});
            skCircle(sketch, "E4.62.0.31", {"center": v(285, -285) * mm, "radius": 0.75 * mm});
            skCircle(sketch, "E4.64.0.31", {"center": v(300, -285) * mm, "radius": 0.75 * mm});
            skCircle(sketch, "E4.66.0.31", {"center": v(315, -285) * mm, "radius": 0.75 * mm});
            skCircle(sketch, "E4.68.0.31", {"center": v(345, -285) * mm, "radius": 0.75 * mm});
            skCircle(sketch, "E4.70.0.31", {"center": v(330, -285) * mm, "radius": 0.75 * mm});
            skCircle(sketch, "E4.0.0.32", {"center": v(-180, -300) * mm, "radius": 0.75 * mm});
            skCircle(sketch, "E4.2.0.32", {"center": v(-165, -300) * mm, "radius": 0.75 * mm});
            skCircle(sketch, "E4.4.0.32", {"center": v(-150, -300) * mm, "radius": 0.75 * mm});
            skCircle(sketch, "E4.6.0.32", {"center": v(-135, -300) * mm, "radius": 0.75 * mm});
            skCircle(sketch, "E4.8.0.32", {"center": v(-120, -300) * mm, "radius": 0.75 * mm});
            skCircle(sketch, "E4.10.0.32", {"center": v(-105, -300) * mm, "radius": 0.75 * mm});
            skCircle(sketch, "E4.12.0.32", {"center": v(-90, -300) * mm, "radius": 0.75 * mm});
            skCircle(sketch, "E4.14.0.32", {"center": v(-75, -300) * mm, "radius": 0.75 * mm});
            skCircle(sketch, "E4.16.0.32", {"center": v(-60, -300) * mm, "radius": 0.75 * mm});
            skCircle(sketch, "E4.18.0.32", {"center": v(-45, -300) * mm, "radius": 0.75 * mm});
            skCircle(sketch, "E4.20.0.32", {"center": v(-30, -300) * mm, "radius": 0.75 * mm});
            skCircle(sketch, "E4.22.0.32", {"center": v(-15, -300) * mm, "radius": 0.75 * mm});
            skCircle(sketch, "E4.24.0.32", {"center": v(0, -300) * mm, "radius": 0.75 * mm});
            skCircle(sketch, "E4.26.0.32", {"center": v(15, -300) * mm, "radius": 0.75 * mm});
            skCircle(sketch, "E4.28.0.32", {"center": v(30, -300) * mm, "radius": 0.75 * mm});
            skCircle(sketch, "E4.30.0.32", {"center": v(45, -300) * mm, "radius": 0.75 * mm});
            skCircle(sketch, "E4.32.0.32", {"center": v(60, -300) * mm, "radius": 0.75 * mm});
            skCircle(sketch, "E4.34.0.32", {"center": v(75, -300) * mm, "radius": 0.75 * mm});
            skCircle(sketch, "E4.36.0.32", {"center": v(90, -300) * mm, "radius": 0.75 * mm});
            skCircle(sketch, "E4.38.0.32", {"center": v(105, -300) * mm, "radius": 0.75 * mm});
            skCircle(sketch, "E4.40.0.32", {"center": v(120, -300) * mm, "radius": 0.75 * mm});
            skCircle(sketch, "E4.42.0.32", {"center": v(135, -300) * mm, "radius": 0.75 * mm});
            skCircle(sketch, "E4.44.0.32", {"center": v(150, -300) * mm, "radius": 0.75 * mm});
            skCircle(sketch, "E4.46.0.32", {"center": v(165, -300) * mm, "radius": 0.75 * mm});
            skCircle(sketch, "E4.48.0.32", {"center": v(180, -300) * mm, "radius": 0.75 * mm});
            skCircle(sketch, "E4.50.0.32", {"center": v(195, -300) * mm, "radius": 0.75 * mm});
            skCircle(sketch, "E4.52.0.32", {"center": v(210, -300) * mm, "radius": 0.75 * mm});
            skCircle(sketch, "E4.54.0.32", {"center": v(225, -300) * mm, "radius": 0.75 * mm});
            skCircle(sketch, "E4.56.0.32", {"center": v(240, -300) * mm, "radius": 0.75 * mm});
            skCircle(sketch, "E4.58.0.32", {"center": v(255, -300) * mm, "radius": 0.75 * mm});
            skCircle(sketch, "E4.60.0.32", {"center": v(270, -300) * mm, "radius": 0.75 * mm});
            skCircle(sketch, "E4.62.0.32", {"center": v(285, -300) * mm, "radius": 0.75 * mm});
            skCircle(sketch, "E4.64.0.32", {"center": v(300, -300) * mm, "radius": 0.75 * mm});
            skCircle(sketch, "E4.66.0.32", {"center": v(315, -300) * mm, "radius": 0.75 * mm});
            skCircle(sketch, "E4.68.0.32", {"center": v(345, -300) * mm, "radius": 0.75 * mm});
            skCircle(sketch, "E4.70.0.32", {"center": v(330, -300) * mm, "radius": 0.75 * mm});
            skCircle(sketch, "E4.0.0.33", {"center": v(-180, -315) * mm, "radius": 0.75 * mm});
            skCircle(sketch, "E4.2.0.33", {"center": v(-165, -315) * mm, "radius": 0.75 * mm});
            skCircle(sketch, "E4.4.0.33", {"center": v(-150, -315) * mm, "radius": 0.75 * mm});
            skCircle(sketch, "E4.6.0.33", {"center": v(-135, -315) * mm, "radius": 0.75 * mm});
            skCircle(sketch, "E4.8.0.33", {"center": v(-120, -315) * mm, "radius": 0.75 * mm});
            skCircle(sketch, "E4.10.0.33", {"center": v(-105, -315) * mm, "radius": 0.75 * mm});
            skCircle(sketch, "E4.12.0.33", {"center": v(-90, -315) * mm, "radius": 0.75 * mm});
            skCircle(sketch, "E4.14.0.33", {"center": v(-75, -315) * mm, "radius": 0.75 * mm});
            skCircle(sketch, "E4.16.0.33", {"center": v(-60, -315) * mm, "radius": 0.75 * mm});
            skCircle(sketch, "E4.18.0.33", {"center": v(-45, -315) * mm, "radius": 0.75 * mm});
            skCircle(sketch, "E4.20.0.33", {"center": v(-30, -315) * mm, "radius": 0.75 * mm});
            skCircle(sketch, "E4.22.0.33", {"center": v(-15, -315) * mm, "radius": 0.75 * mm});
            skCircle(sketch, "E4.24.0.33", {"center": v(0, -315) * mm, "radius": 0.75 * mm});
            skCircle(sketch, "E4.26.0.33", {"center": v(15, -315) * mm, "radius": 0.75 * mm});
            skCircle(sketch, "E4.28.0.33", {"center": v(30, -315) * mm, "radius": 0.75 * mm});
            skCircle(sketch, "E4.30.0.33", {"center": v(45, -315) * mm, "radius": 0.75 * mm});
            skCircle(sketch, "E4.32.0.33", {"center": v(60, -315) * mm, "radius": 0.75 * mm});
            skCircle(sketch, "E4.34.0.33", {"center": v(75, -315) * mm, "radius": 0.75 * mm});
            skCircle(sketch, "E4.36.0.33", {"center": v(90, -315) * mm, "radius": 0.75 * mm});
            skCircle(sketch, "E4.38.0.33", {"center": v(105, -315) * mm, "radius": 0.75 * mm});
            skCircle(sketch, "E4.40.0.33", {"center": v(120, -315) * mm, "radius": 0.75 * mm});
            skCircle(sketch, "E4.42.0.33", {"center": v(135, -315) * mm, "radius": 0.75 * mm});
            skCircle(sketch, "E4.44.0.33", {"center": v(150, -315) * mm, "radius": 0.75 * mm});
            skCircle(sketch, "E4.46.0.33", {"center": v(165, -315) * mm, "radius": 0.75 * mm});
            skCircle(sketch, "E4.48.0.33", {"center": v(180, -315) * mm, "radius": 0.75 * mm});
            skCircle(sketch, "E4.50.0.33", {"center": v(195, -315) * mm, "radius": 0.75 * mm});
            skCircle(sketch, "E4.52.0.33", {"center": v(210, -315) * mm, "radius": 0.75 * mm});
            skCircle(sketch, "E4.54.0.33", {"center": v(225, -315) * mm, "radius": 0.75 * mm});
            skCircle(sketch, "E4.56.0.33", {"center": v(240, -315) * mm, "radius": 0.75 * mm});
            skCircle(sketch, "E4.58.0.33", {"center": v(255, -315) * mm, "radius": 0.75 * mm});
            skCircle(sketch, "E4.60.0.33", {"center": v(270, -315) * mm, "radius": 0.75 * mm});
            skCircle(sketch, "E4.62.0.33", {"center": v(285, -315) * mm, "radius": 0.75 * mm});
            skCircle(sketch, "E4.64.0.33", {"center": v(300, -315) * mm, "radius": 0.75 * mm});
            skCircle(sketch, "E4.66.0.33", {"center": v(315, -315) * mm, "radius": 0.75 * mm});
            skCircle(sketch, "E4.68.0.33", {"center": v(345, -315) * mm, "radius": 0.75 * mm});
            skCircle(sketch, "E4.70.0.33", {"center": v(330, -315) * mm, "radius": 0.75 * mm});
            skCircle(sketch, "E4.0.0.34", {"center": v(-180, -330) * mm, "radius": 0.75 * mm});
            skCircle(sketch, "E4.2.0.34", {"center": v(-165, -330) * mm, "radius": 0.75 * mm});
            skCircle(sketch, "E4.4.0.34", {"center": v(-150, -330) * mm, "radius": 0.75 * mm});
            skCircle(sketch, "E4.6.0.34", {"center": v(-135, -330) * mm, "radius": 0.75 * mm});
            skCircle(sketch, "E4.8.0.34", {"center": v(-120, -330) * mm, "radius": 0.75 * mm});
            skCircle(sketch, "E4.10.0.34", {"center": v(-105, -330) * mm, "radius": 0.75 * mm});
            skCircle(sketch, "E4.12.0.34", {"center": v(-90, -330) * mm, "radius": 0.75 * mm});
            skCircle(sketch, "E4.14.0.34", {"center": v(-75, -330) * mm, "radius": 0.75 * mm});
            skCircle(sketch, "E4.16.0.34", {"center": v(-60, -330) * mm, "radius": 0.75 * mm});
            skCircle(sketch, "E4.18.0.34", {"center": v(-45, -330) * mm, "radius": 0.75 * mm});
            skCircle(sketch, "E4.20.0.34", {"center": v(-30, -330) * mm, "radius": 0.75 * mm});
            skCircle(sketch, "E4.22.0.34", {"center": v(-15, -330) * mm, "radius": 0.75 * mm});
            skCircle(sketch, "E4.24.0.34", {"center": v(0, -330) * mm, "radius": 0.75 * mm});
            skCircle(sketch, "E4.26.0.34", {"center": v(15, -330) * mm, "radius": 0.75 * mm});
            skCircle(sketch, "E4.28.0.34", {"center": v(30, -330) * mm, "radius": 0.75 * mm});
            skCircle(sketch, "E4.30.0.34", {"center": v(45, -330) * mm, "radius": 0.75 * mm});
            skCircle(sketch, "E4.32.0.34", {"center": v(60, -330) * mm, "radius": 0.75 * mm});
            skCircle(sketch, "E4.34.0.34", {"center": v(75, -330) * mm, "radius": 0.75 * mm});
            skCircle(sketch, "E4.36.0.34", {"center": v(90, -330) * mm, "radius": 0.75 * mm});
            skCircle(sketch, "E4.38.0.34", {"center": v(105, -330) * mm, "radius": 0.75 * mm});
            skCircle(sketch, "E4.40.0.34", {"center": v(120, -330) * mm, "radius": 0.75 * mm});
            skCircle(sketch, "E4.42.0.34", {"center": v(135, -330) * mm, "radius": 0.75 * mm});
            skCircle(sketch, "E4.44.0.34", {"center": v(150, -330) * mm, "radius": 0.75 * mm});
            skCircle(sketch, "E4.46.0.34", {"center": v(165, -330) * mm, "radius": 0.75 * mm});
            skCircle(sketch, "E4.48.0.34", {"center": v(180, -330) * mm, "radius": 0.75 * mm});
            skCircle(sketch, "E4.50.0.34", {"center": v(195, -330) * mm, "radius": 0.75 * mm});
            skCircle(sketch, "E4.52.0.34", {"center": v(210, -330) * mm, "radius": 0.75 * mm});
            skCircle(sketch, "E4.54.0.34", {"center": v(225, -330) * mm, "radius": 0.75 * mm});
            skCircle(sketch, "E4.56.0.34", {"center": v(240, -330) * mm, "radius": 0.75 * mm});
            skCircle(sketch, "E4.58.0.34", {"center": v(255, -330) * mm, "radius": 0.75 * mm});
            skCircle(sketch, "E4.60.0.34", {"center": v(270, -330) * mm, "radius": 0.75 * mm});
            skCircle(sketch, "E4.62.0.34", {"center": v(285, -330) * mm, "radius": 0.75 * mm});
            skCircle(sketch, "E4.64.0.34", {"center": v(300, -330) * mm, "radius": 0.75 * mm});
            skCircle(sketch, "E4.66.0.34", {"center": v(315, -330) * mm, "radius": 0.75 * mm});
            skCircle(sketch, "E4.68.0.34", {"center": v(345, -330) * mm, "radius": 0.75 * mm});
            skCircle(sketch, "E4.70.0.34", {"center": v(330, -330) * mm, "radius": 0.75 * mm});
            skCircle(sketch, "E4.0.0.35", {"center": v(-180, -345) * mm, "radius": 0.75 * mm});
            skCircle(sketch, "E4.2.0.35", {"center": v(-165, -345) * mm, "radius": 0.75 * mm});
            skCircle(sketch, "E4.4.0.35", {"center": v(-150, -345) * mm, "radius": 0.75 * mm});
            skCircle(sketch, "E4.6.0.35", {"center": v(-135, -345) * mm, "radius": 0.75 * mm});
            skCircle(sketch, "E4.8.0.35", {"center": v(-120, -345) * mm, "radius": 0.75 * mm});
            skCircle(sketch, "E4.10.0.35", {"center": v(-105, -345) * mm, "radius": 0.75 * mm});
            skCircle(sketch, "E4.12.0.35", {"center": v(-90, -345) * mm, "radius": 0.75 * mm});
            skCircle(sketch, "E4.14.0.35", {"center": v(-75, -345) * mm, "radius": 0.75 * mm});
            skCircle(sketch, "E4.16.0.35", {"center": v(-60, -345) * mm, "radius": 0.75 * mm});
            skCircle(sketch, "E4.18.0.35", {"center": v(-45, -345) * mm, "radius": 0.75 * mm});
            skCircle(sketch, "E4.20.0.35", {"center": v(-30, -345) * mm, "radius": 0.75 * mm});
            skCircle(sketch, "E4.22.0.35", {"center": v(-15, -345) * mm, "radius": 0.75 * mm});
            skCircle(sketch, "E4.24.0.35", {"center": v(0, -345) * mm, "radius": 0.75 * mm});
            skCircle(sketch, "E4.26.0.35", {"center": v(15, -345) * mm, "radius": 0.75 * mm});
            skCircle(sketch, "E4.28.0.35", {"center": v(30, -345) * mm, "radius": 0.75 * mm});
            skCircle(sketch, "E4.30.0.35", {"center": v(45, -345) * mm, "radius": 0.75 * mm});
            skCircle(sketch, "E4.32.0.35", {"center": v(60, -345) * mm, "radius": 0.75 * mm});
            skCircle(sketch, "E4.34.0.35", {"center": v(75, -345) * mm, "radius": 0.75 * mm});
            skCircle(sketch, "E4.36.0.35", {"center": v(90, -345) * mm, "radius": 0.75 * mm});
            skCircle(sketch, "E4.38.0.35", {"center": v(105, -345) * mm, "radius": 0.75 * mm});
            skCircle(sketch, "E4.40.0.35", {"center": v(120, -345) * mm, "radius": 0.75 * mm});
            skCircle(sketch, "E4.42.0.35", {"center": v(135, -345) * mm, "radius": 0.75 * mm});
            skCircle(sketch, "E4.44.0.35", {"center": v(150, -345) * mm, "radius": 0.75 * mm});
            skCircle(sketch, "E4.46.0.35", {"center": v(165, -345) * mm, "radius": 0.75 * mm});
            skCircle(sketch, "E4.48.0.35", {"center": v(180, -345) * mm, "radius": 0.75 * mm});
            skCircle(sketch, "E4.50.0.35", {"center": v(195, -345) * mm, "radius": 0.75 * mm});
            skCircle(sketch, "E4.52.0.35", {"center": v(210, -345) * mm, "radius": 0.75 * mm});
            skCircle(sketch, "E4.54.0.35", {"center": v(225, -345) * mm, "radius": 0.75 * mm});
            skCircle(sketch, "E4.56.0.35", {"center": v(240, -345) * mm, "radius": 0.75 * mm});
            skCircle(sketch, "E4.58.0.35", {"center": v(255, -345) * mm, "radius": 0.75 * mm});
            skCircle(sketch, "E4.60.0.35", {"center": v(270, -345) * mm, "radius": 0.75 * mm});
            skCircle(sketch, "E4.62.0.35", {"center": v(285, -345) * mm, "radius": 0.75 * mm});
            skCircle(sketch, "E4.64.0.35", {"center": v(300, -345) * mm, "radius": 0.75 * mm});
            skCircle(sketch, "E4.66.0.35", {"center": v(315, -345) * mm, "radius": 0.75 * mm});
            skCircle(sketch, "E4.68.0.35", {"center": v(345, -345) * mm, "radius": 0.75 * mm});
            skCircle(sketch, "E4.70.0.35", {"center": v(330, -345) * mm, "radius": 0.75 * mm});
            skCircle(sketch, "E4.0.0.36", {"center": v(-180, -360) * mm, "radius": 0.75 * mm});
            skCircle(sketch, "E4.2.0.36", {"center": v(-165, -360) * mm, "radius": 0.75 * mm});
            skCircle(sketch, "E4.4.0.36", {"center": v(-150, -360) * mm, "radius": 0.75 * mm});
            skCircle(sketch, "E4.6.0.36", {"center": v(-135, -360) * mm, "radius": 0.75 * mm});
            skCircle(sketch, "E4.8.0.36", {"center": v(-120, -360) * mm, "radius": 0.75 * mm});
            skCircle(sketch, "E4.10.0.36", {"center": v(-105, -360) * mm, "radius": 0.75 * mm});
            skCircle(sketch, "E4.12.0.36", {"center": v(-90, -360) * mm, "radius": 0.75 * mm});
            skCircle(sketch, "E4.14.0.36", {"center": v(-75, -360) * mm, "radius": 0.75 * mm});
            skCircle(sketch, "E4.16.0.36", {"center": v(-60, -360) * mm, "radius": 0.75 * mm});
            skCircle(sketch, "E4.18.0.36", {"center": v(-45, -360) * mm, "radius": 0.75 * mm});
            skCircle(sketch, "E4.20.0.36", {"center": v(-30, -360) * mm, "radius": 0.75 * mm});
            skCircle(sketch, "E4.22.0.36", {"center": v(-15, -360) * mm, "radius": 0.75 * mm});
            skCircle(sketch, "E4.24.0.36", {"center": v(0, -360) * mm, "radius": 0.75 * mm});
            skCircle(sketch, "E4.26.0.36", {"center": v(15, -360) * mm, "radius": 0.75 * mm});
            skCircle(sketch, "E4.28.0.36", {"center": v(30, -360) * mm, "radius": 0.75 * mm});
            skCircle(sketch, "E4.30.0.36", {"center": v(45, -360) * mm, "radius": 0.75 * mm});
            skCircle(sketch, "E4.32.0.36", {"center": v(60, -360) * mm, "radius": 0.75 * mm});
            skCircle(sketch, "E4.34.0.36", {"center": v(75, -360) * mm, "radius": 0.75 * mm});
            skCircle(sketch, "E4.36.0.36", {"center": v(90, -360) * mm, "radius": 0.75 * mm});
            skCircle(sketch, "E4.38.0.36", {"center": v(105, -360) * mm, "radius": 0.75 * mm});
            skCircle(sketch, "E4.40.0.36", {"center": v(120, -360) * mm, "radius": 0.75 * mm});
            skCircle(sketch, "E4.42.0.36", {"center": v(135, -360) * mm, "radius": 0.75 * mm});
            skCircle(sketch, "E4.44.0.36", {"center": v(150, -360) * mm, "radius": 0.75 * mm});
            skCircle(sketch, "E4.46.0.36", {"center": v(165, -360) * mm, "radius": 0.75 * mm});
            skCircle(sketch, "E4.48.0.36", {"center": v(180, -360) * mm, "radius": 0.75 * mm});
            skCircle(sketch, "E4.50.0.36", {"center": v(195, -360) * mm, "radius": 0.75 * mm});
            skCircle(sketch, "E4.52.0.36", {"center": v(210, -360) * mm, "radius": 0.75 * mm});
            skCircle(sketch, "E4.54.0.36", {"center": v(225, -360) * mm, "radius": 0.75 * mm});
            skCircle(sketch, "E4.56.0.36", {"center": v(240, -360) * mm, "radius": 0.75 * mm});
            skCircle(sketch, "E4.58.0.36", {"center": v(255, -360) * mm, "radius": 0.75 * mm});
            skCircle(sketch, "E4.60.0.36", {"center": v(270, -360) * mm, "radius": 0.75 * mm});
            skCircle(sketch, "E4.62.0.36", {"center": v(285, -360) * mm, "radius": 0.75 * mm});
            skCircle(sketch, "E4.64.0.36", {"center": v(300, -360) * mm, "radius": 0.75 * mm});
            skCircle(sketch, "E4.66.0.36", {"center": v(315, -360) * mm, "radius": 0.75 * mm});
            skCircle(sketch, "E4.68.0.36", {"center": v(345, -360) * mm, "radius": 0.75 * mm});
            skCircle(sketch, "E4.70.0.36", {"center": v(330, -360) * mm, "radius": 0.75 * mm});
            skCircle(sketch, "E5.0.36.0", {"center": v(360, 180) * mm, "radius": 0.75 * mm});
            skCircle(sketch, "E6.0.1.0", {"center": v(360, 170) * mm, "radius": 0.75 * mm});
            skCircle(sketch, "E6.0.2.0", {"center": v(360, 160) * mm, "radius": 0.75 * mm});
            skCircle(sketch, "E6.0.3.0", {"center": v(360, 150) * mm, "radius": 0.75 * mm});
            skCircle(sketch, "E6.0.4.0", {"center": v(360, 140) * mm, "radius": 0.75 * mm});
            skCircle(sketch, "E6.0.5.0", {"center": v(360, 130) * mm, "radius": 0.75 * mm});
            skCircle(sketch, "E6.0.6.0", {"center": v(360, 120) * mm, "radius": 0.75 * mm});
            skCircle(sketch, "E6.0.7.0", {"center": v(360, 110) * mm, "radius": 0.75 * mm});
            skCircle(sketch, "E6.0.8.0", {"center": v(360, 100) * mm, "radius": 0.75 * mm});
            skCircle(sketch, "E6.0.9.0", {"center": v(360, 90) * mm, "radius": 0.75 * mm});
            skCircle(sketch, "E6.0.10.0", {"center": v(360, 80) * mm, "radius": 0.75 * mm});
            skCircle(sketch, "E6.0.11.0", {"center": v(360, 70) * mm, "radius": 0.75 * mm});
            skCircle(sketch, "E6.0.12.0", {"center": v(360, 60) * mm, "radius": 0.75 * mm});
            skCircle(sketch, "E6.0.13.0", {"center": v(360, 50) * mm, "radius": 0.75 * mm});
            skCircle(sketch, "E6.0.14.0", {"center": v(360, 40) * mm, "radius": 0.75 * mm});
            skCircle(sketch, "E6.0.15.0", {"center": v(360, 30) * mm, "radius": 0.75 * mm});
            skCircle(sketch, "E6.0.16.0", {"center": v(360, 20) * mm, "radius": 0.75 * mm});
            skCircle(sketch, "E6.0.17.0", {"center": v(360, 10) * mm, "radius": 0.75 * mm});
            skCircle(sketch, "E6.0.18.0", {"center": v(360, 0) * mm, "radius": 0.75 * mm});
            skCircle(sketch, "E6.0.19.0", {"center": v(360, -10) * mm, "radius": 0.75 * mm});
            skCircle(sketch, "E6.0.20.0", {"center": v(360, -20) * mm, "radius": 0.75 * mm});
            skCircle(sketch, "E6.0.21.0", {"center": v(360, -30) * mm, "radius": 0.75 * mm});
            skCircle(sketch, "E6.0.22.0", {"center": v(360, -40) * mm, "radius": 0.75 * mm});
            skCircle(sketch, "E6.0.23.0", {"center": v(360, -50) * mm, "radius": 0.75 * mm});
            skCircle(sketch, "E6.0.24.0", {"center": v(360, -60) * mm, "radius": 0.75 * mm});
            skCircle(sketch, "E6.0.25.0", {"center": v(360, -70) * mm, "radius": 0.75 * mm});
            skCircle(sketch, "E6.0.26.0", {"center": v(360, -80) * mm, "radius": 0.75 * mm});
            skCircle(sketch, "E6.0.27.0", {"center": v(360, -90) * mm, "radius": 0.75 * mm});
            skCircle(sketch, "E6.0.28.0", {"center": v(360, -100) * mm, "radius": 0.75 * mm});
            skCircle(sketch, "E6.0.29.0", {"center": v(360, -110) * mm, "radius": 0.75 * mm});
            skCircle(sketch, "E6.0.30.0", {"center": v(360, -120) * mm, "radius": 0.75 * mm});
            skCircle(sketch, "E6.0.31.0", {"center": v(360, -130) * mm, "radius": 0.75 * mm});
            skCircle(sketch, "E6.0.32.0", {"center": v(360, -140) * mm, "radius": 0.75 * mm});
            skCircle(sketch, "E6.0.33.0", {"center": v(360, -150) * mm, "radius": 0.75 * mm});
            skCircle(sketch, "E6.0.34.0", {"center": v(360, -160) * mm, "radius": 0.75 * mm});
            skCircle(sketch, "E6.0.35.0", {"center": v(360, -170) * mm, "radius": 0.75 * mm});
            skCircle(sketch, "E6.0.36.0", {"center": v(360, -180) * mm, "radius": 0.75 * mm});
            skLineSegment(sketch, "E6.direction1", {"start": v(360, 180) * mm, "end": v(385, 180) * mm, "construction": true});
            skLineSegment(sketch, "E6.direction2", {"start": v(360, 180) * mm, "end": v(360, 170) * mm, "construction": true});
            skSolve(sketch);
        }
        {
            var Q0;
            Q0 = qSketchRegion(id + "F2", true);
            extrude(context, id + "F3", {"entities" : qUnion([Q0]), "operationType" : NewBodyOperationType.REMOVE, "oppositeDirection" : true, "depth" : 25 * mm, "offsetDistance" : 25 * mm});
        }
        {
            var Q0;
            Q0=makeQuery(id+"F1.opExtrude","CAP_FACE",FACE,{"disambiguationData":[OSD([sQuery(id+"F0.wireOp",EDGE,"E0.bottom"),sQuery(id+"F0.wireOp",EDGE,"E0.top"),sQuery(id+"F0.wireOp",EDGE,"E0.left"),sQuery(id+"F0.wireOp",EDGE,"E0.right")])],"isStart":false});
            var sketch = newSketch(context, id + "F4", { "sketchPlane" : qUnion([Q0])});
            skLineSegment(sketch, "E7.bottom", {"start": v(-4.82, 5.38) * mm, "end": v(5.21, 5.38) * mm});
            skLineSegment(sketch, "E7.top", {"start": v(-4.82, -6.3) * mm, "end": v(5.21, -6.3) * mm});
            skLineSegment(sketch, "E7.left", {"start": v(-4.82, 5.38) * mm, "end": v(-4.82, -6.3) * mm});
            skLineSegment(sketch, "E7.right", {"start": v(5.21, 5.38) * mm, "end": v(5.21, -6.3) * mm});
            skSolve(sketch);
        }
        {
            var Q0;
            Q0 = qSketchRegion(id + "F4", true);
            extrude(context, id + "F5", {"entities" : qUnion([Q0]), "operationType" : NewBodyOperationType.ADD, "oppositeDirection" : true, "depth" : 1 * mm, "offsetDistance" : 25 * mm});
        }
    });
